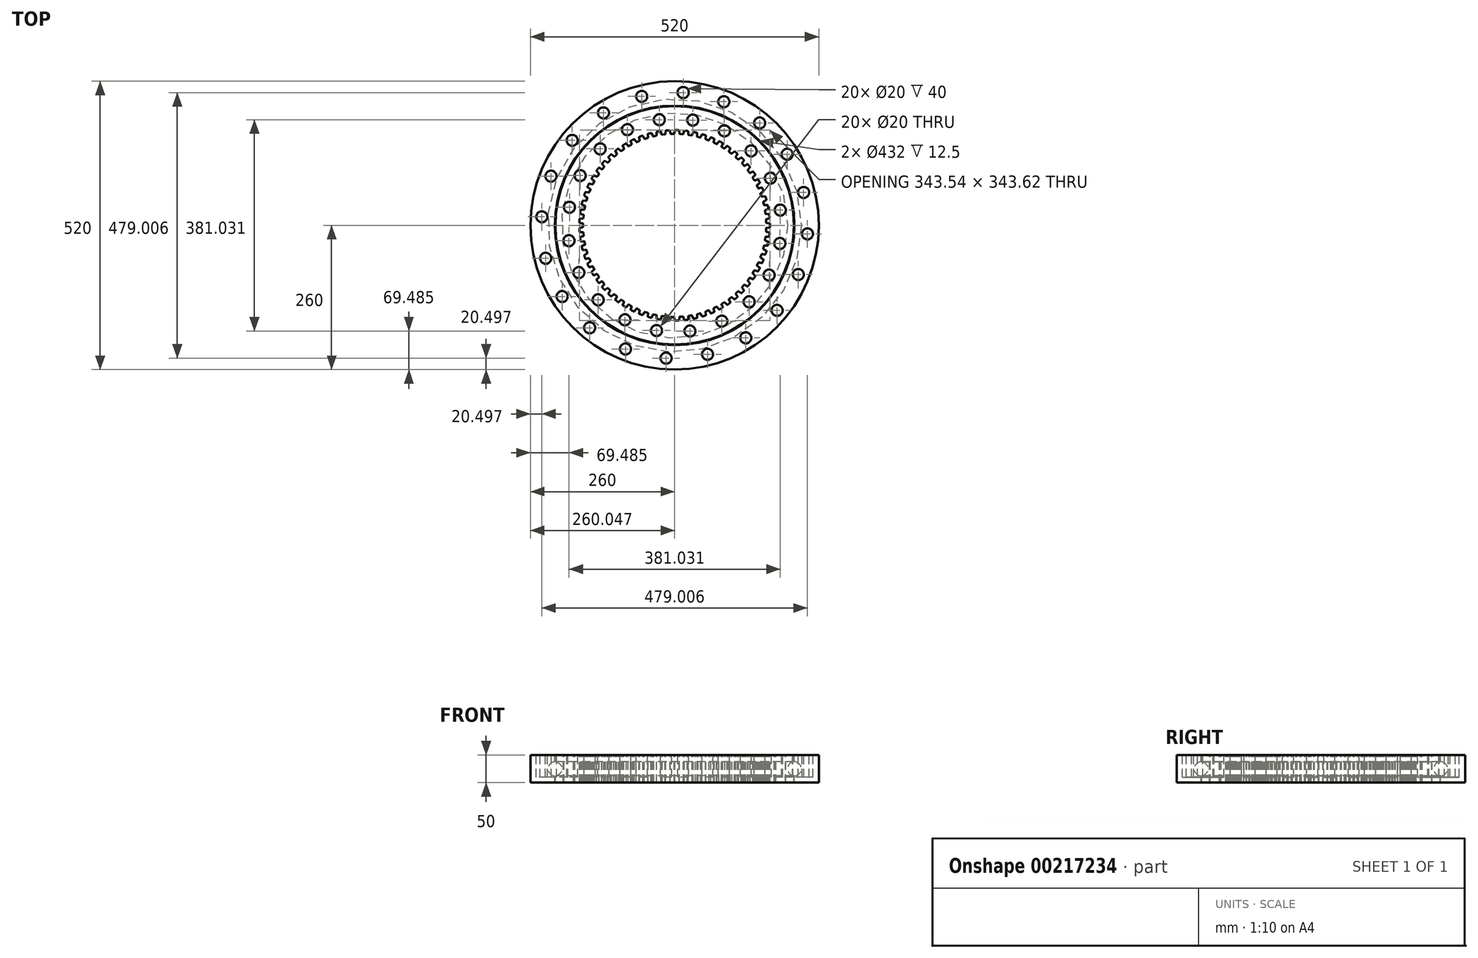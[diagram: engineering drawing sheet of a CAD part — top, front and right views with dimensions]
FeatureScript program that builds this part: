
annotation { "Feature Type Name" : "Feature", "Feature Type Description" : "" }
export const myFeature = defineFeature(function(context is Context, id is Id, definition is map)
    precondition{}
    {
        {
            var Q0;
            Q0=qCreatedBy(makeId("Front.planeOp"),FACE);
            var sketch = newSketch(context, id + "F0", { "sketchPlane" : qUnion([Q0])});
            skLineSegment(sketch, "E0.bottom", {"start": v(-260, 25) * mm, "end": v(-216, 25) * mm});
            skLineSegment(sketch, "E0.top", {"start": v(-260, -25) * mm, "end": v(-216, -25) * mm});
            skLineSegment(sketch, "E0.left", {"start": v(-260, 25) * mm, "end": v(-260, -25) * mm});
            skLineSegment(sketch, "E0.right", {"start": v(-216, 25) * mm, "end": v(-216, 12.5) * mm});
            skPoint(sketch, "E0.middle", {"position": v(-238, 0) * mm});
            skArc(sketch, "E1", {"start": v(-216, 12.5) * mm, "mid": v(-228.5, 0) * mm, "end": v(-216, -12.5) * mm});
            skLineSegment(sketch, "E2.bottom", {"start": v(-215, 25) * mm, "end": v(-172, 25) * mm});
            skLineSegment(sketch, "E2.top", {"start": v(-215, -25) * mm, "end": v(-172, -25) * mm});
            skLineSegment(sketch, "E2.left", {"start": v(-215, 25) * mm, "end": v(-215, 12.46) * mm});
            skLineSegment(sketch, "E2.right", {"start": v(-172, 25) * mm, "end": v(-172, -25) * mm});
            skPoint(sketch, "E2.middle", {"position": v(-193.5, 0) * mm});
            skArc(sketch, "E3.trimOffspring", {"start": v(-215, -12.46) * mm, "mid": v(-203.5, 0) * mm, "end": v(-215, 12.46) * mm});
            skLineSegment(sketch, "E4.trimOffspring", {"start": v(-215, -12.46) * mm, "end": v(-215, -25) * mm});
            skLineSegment(sketch, "E5.trimOffspring", {"start": v(-216, -12.5) * mm, "end": v(-216, -25) * mm});
            skLineSegment(sketch, "E6", {"start": v(0, 47.87) * mm, "end": v(0, -50.9) * mm, "construction": true});
            skSolve(sketch);
        }
        {
            var Q0;
            Q0=makeQuery(id+"F0.imprint","IMPRINT",FACE,{"disambiguationData":[TD([[makeQuery(id+"F0.imprint","IMPRINT",EDGE,{"derivedFrom":sQuery(id+"F0.wireOp",EDGE,"E0.bottom")}),-1.0]])]});
            var Q1;
            Q1=makeQuery(id+"F0.imprint","IMPRINT",FACE,{"disambiguationData":[TD([[makeQuery(id+"F0.imprint","IMPRINT",EDGE,{"derivedFrom":sQuery(id+"F0.wireOp",EDGE,"E2.bottom")}),-1.0]])]});
            var Q2;
            Q2=sQuery(id+"F0.wireOp",EDGE,"E6");
            revolve(context, id + "F1", {"entities" : qUnion([Q0, Q1]), "axis" : qUnion([Q2]), "revolveType" : RevolveType.FULL});
        }
        {
            var Q0;
            Q0=makeQuery(id+"F1.opRevolve","SWEPT_FACE",FACE,{"disambiguationData":[OSD([sQuery(id+"F0.wireOp",EDGE,"E0.bottom")])]});
            var sketch = newSketch(context, id + "F2", { "sketchPlane" : qUnion([Q0])});
            skCircle(sketch, "E7", {"center": v(0, 0) * mm, "radius": 240 * mm, "construction": true});
            skCircle(sketch, "E8", {"center": v(-239.5, 15.44) * mm, "radius": 10 * mm});
            skCircle(sketch, "E9.1.0", {"center": v(-232.55, -59.32) * mm, "radius": 10 * mm});
            skCircle(sketch, "E9.2.0", {"center": v(-202.84, -128.28) * mm, "radius": 10 * mm});
            skCircle(sketch, "E9.3.0", {"center": v(-153.27, -184.69) * mm, "radius": 10 * mm});
            skCircle(sketch, "E9.4.0", {"center": v(-88.7, -223) * mm, "radius": 10 * mm});
            skCircle(sketch, "E9.5.0", {"center": v(-15.44, -239.5) * mm, "radius": 10 * mm});
            skCircle(sketch, "E9.6.0", {"center": v(59.32, -232.55) * mm, "radius": 10 * mm});
            skCircle(sketch, "E9.7.0", {"center": v(128.28, -202.84) * mm, "radius": 10 * mm});
            skCircle(sketch, "E9.8.0", {"center": v(184.69, -153.27) * mm, "radius": 10 * mm});
            skCircle(sketch, "E9.9.0", {"center": v(223, -88.7) * mm, "radius": 10 * mm});
            skCircle(sketch, "E9.10.0", {"center": v(239.5, -15.44) * mm, "radius": 10 * mm});
            skCircle(sketch, "E9.11.0", {"center": v(232.55, 59.32) * mm, "radius": 10 * mm});
            skCircle(sketch, "E9.12.0", {"center": v(202.84, 128.28) * mm, "radius": 10 * mm});
            skCircle(sketch, "E9.13.0", {"center": v(153.27, 184.69) * mm, "radius": 10 * mm});
            skCircle(sketch, "E9.14.0", {"center": v(88.7, 223) * mm, "radius": 10 * mm});
            skCircle(sketch, "E9.15.0", {"center": v(15.44, 239.5) * mm, "radius": 10 * mm});
            skCircle(sketch, "E9.16.0", {"center": v(-59.32, 232.55) * mm, "radius": 10 * mm});
            skCircle(sketch, "E9.17.0", {"center": v(-128.28, 202.84) * mm, "radius": 10 * mm});
            skCircle(sketch, "E9.18.0", {"center": v(-184.69, 153.27) * mm, "radius": 10 * mm});
            skCircle(sketch, "E9.19.0", {"center": v(-223, 88.7) * mm, "radius": 10 * mm});
            skSolve(sketch);
        }
        {
            var Q0;
            Q0 = qSketchRegion(id + "F2", true);
            extrude(context, id + "F3", {"entities" : qUnion([Q0]), "operationType" : NewBodyOperationType.REMOVE, "oppositeDirection" : true, "depth" : 40 * mm});
        }
        {
            var Q0;
            Q0=makeQuery(id+"F1.opRevolve","SWEPT_FACE",FACE,{"disambiguationData":[OSD([sQuery(id+"F0.wireOp",EDGE,"E2.bottom")])]});
            var sketch = newSketch(context, id + "F4", { "sketchPlane" : qUnion([Q0])});
            skCircle(sketch, "E10", {"center": v(0, 0) * mm, "radius": 192.5 * mm, "construction": true});
            skCircle(sketch, "E11", {"center": v(-189.71, 32.65) * mm, "radius": 10 * mm});
            skCircle(sketch, "E12.1.0", {"center": v(-190.52, -27.57) * mm, "radius": 10 * mm});
            skCircle(sketch, "E12.2.0", {"center": v(-172.67, -85.1) * mm, "radius": 10 * mm});
            skCircle(sketch, "E12.3.0", {"center": v(-137.92, -134.29) * mm, "radius": 10 * mm});
            skCircle(sketch, "E12.4.0", {"center": v(-89.68, -170.34) * mm, "radius": 10 * mm});
            skCircle(sketch, "E12.5.0", {"center": v(-32.65, -189.71) * mm, "radius": 10 * mm});
            skCircle(sketch, "E12.6.0", {"center": v(27.57, -190.52) * mm, "radius": 10 * mm});
            skCircle(sketch, "E12.7.0", {"center": v(85.1, -172.67) * mm, "radius": 10 * mm});
            skCircle(sketch, "E12.8.0", {"center": v(134.29, -137.92) * mm, "radius": 10 * mm});
            skCircle(sketch, "E12.9.0", {"center": v(170.34, -89.68) * mm, "radius": 10 * mm});
            skCircle(sketch, "E12.10.0", {"center": v(189.71, -32.65) * mm, "radius": 10 * mm});
            skCircle(sketch, "E12.11.0", {"center": v(190.52, 27.57) * mm, "radius": 10 * mm});
            skCircle(sketch, "E12.12.0", {"center": v(172.67, 85.1) * mm, "radius": 10 * mm});
            skCircle(sketch, "E12.13.0", {"center": v(137.92, 134.29) * mm, "radius": 10 * mm});
            skCircle(sketch, "E12.14.0", {"center": v(89.68, 170.34) * mm, "radius": 10 * mm});
            skCircle(sketch, "E12.15.0", {"center": v(32.65, 189.71) * mm, "radius": 10 * mm});
            skCircle(sketch, "E12.16.0", {"center": v(-27.57, 190.52) * mm, "radius": 10 * mm});
            skCircle(sketch, "E12.17.0", {"center": v(-85.1, 172.67) * mm, "radius": 10 * mm});
            skCircle(sketch, "E12.18.0", {"center": v(-134.29, 137.92) * mm, "radius": 10 * mm});
            skCircle(sketch, "E12.19.0", {"center": v(-170.34, 89.68) * mm, "radius": 10 * mm});
            skSolve(sketch);
        }
        {
            var Q0;
            Q0 = qSketchRegion(id + "F4", true);
            extrude(context, id + "F5", {"entities" : qUnion([Q0]), "operationType" : NewBodyOperationType.REMOVE, "endBound" : BoundingType.THROUGH_ALL, "oppositeDirection" : true, "depth" : 25 * mm});
        }
        {
            var Q0;
            Q0=makeQuery(id+"F1.opRevolve","SWEPT_FACE",FACE,{"disambiguationData":[OSD([sQuery(id+"F0.wireOp",EDGE,"E2.bottom")])]});
            var sketch = newSketch(context, id + "F6", { "sketchPlane" : qUnion([Q0])});
            skLineSegment(sketch, "E13.left", {"start": v(-165.08, -2.5) * mm, "end": v(-165.08, 2.5) * mm});
            skPoint(sketch, "E13.middle", {"position": v(-168.03, 0) * mm});
            skArc(sketch, "E14", {"start": v(-171.72, -5.68) * mm, "mid": v(-171.62, -8.3) * mm, "end": v(-171.47, -10.92) * mm});
            skArc(sketch, "E15", {"start": v(-171.72, 5.68) * mm, "mid": v(-171.62, 5.05) * mm, "end": v(-171.29, 4.5) * mm});
            skPoint(sketch, "E16.visualSharp", {"position": v(-165.08, 5.92) * mm});
            skArc(sketch, "E16.filletArc", {"start": v(-165.08, 2.5) * mm, "mid": v(-165.38, 3.2) * mm, "end": v(-166.08, 3.5) * mm});
            skArc(sketch, "E17.filletArc", {"start": v(-166.08, -3.5) * mm, "mid": v(-165.38, -3.2) * mm, "end": v(-165.08, -2.5) * mm});
            skLineSegment(sketch, "E18", {"start": v(-170.94, 0) * mm, "end": v(-163.27, 0) * mm, "construction": true});
            skArc(sketch, "E19.MirrorCS", {"start": v(-171.72, -5.68) * mm, "mid": v(-171.62, -5.05) * mm, "end": v(-171.29, -4.5) * mm});
            skLineSegment(sketch, "E20", {"start": v(-171.29, 4.5) * mm, "end": v(-166.08, 3.5) * mm});
            skLineSegment(sketch, "E21", {"start": v(-171.29, -4.5) * mm, "end": v(-166.08, -3.5) * mm});
            skCircle(sketch, "E22", {"center": v(0, 0) * mm, "radius": 178.55 * mm});
            skPoint(sketch, "E23.1.0", {"position": v(-164.88, -10.04) * mm});
            skLineSegment(sketch, "E23.1.1", {"start": v(-170.92, -12.05) * mm, "end": v(-165.65, -12.55) * mm});
            skPoint(sketch, "E23.1.2", {"position": v(-164.2, -17.13) * mm});
            skArc(sketch, "E23.1.3", {"start": v(-170.37, -22.23) * mm, "mid": v(-170.33, -21.59) * mm, "end": v(-170.05, -21.01) * mm});
            skArc(sketch, "E23.1.4", {"start": v(-171.47, -10.92) * mm, "mid": v(-171.3, -11.54) * mm, "end": v(-170.92, -12.05) * mm});
            skPoint(sketch, "E23.1.5", {"position": v(-167.25, -16.22) * mm});
            skLineSegment(sketch, "E23.1.6", {"start": v(-170.05, -21.01) * mm, "end": v(-164.97, -19.51) * mm});
            skPoint(sketch, "E23.1.7", {"position": v(-169.6, -22.4) * mm});
            skPoint(sketch, "E23.1.8", {"position": v(-170.3, -15.3) * mm});
            skLineSegment(sketch, "E23.1.9", {"start": v(-164.07, -18.42) * mm, "end": v(-164.56, -13.44) * mm});
            skArc(sketch, "E23.1.10", {"start": v(-164.56, -13.44) * mm, "mid": v(-164.91, -12.77) * mm, "end": v(-165.65, -12.55) * mm});
            skArc(sketch, "E23.1.11", {"start": v(-164.97, -19.51) * mm, "mid": v(-164.3, -19.15) * mm, "end": v(-164.07, -18.42) * mm});
            skPoint(sketch, "E23.2.0", {"position": v(-163.15, -25.91) * mm});
            skLineSegment(sketch, "E23.2.1", {"start": v(-168.96, -28.5) * mm, "end": v(-163.66, -28.47) * mm});
            skPoint(sketch, "E23.2.2", {"position": v(-161.78, -32.9) * mm});
            skArc(sketch, "E23.2.3", {"start": v(-167.43, -38.57) * mm, "mid": v(-167.46, -37.93) * mm, "end": v(-167.23, -37.33) * mm});
            skArc(sketch, "E23.2.4", {"start": v(-169.62, -27.42) * mm, "mid": v(-169.4, -28.02) * mm, "end": v(-168.96, -28.5) * mm});
            skPoint(sketch, "E23.2.5", {"position": v(-164.9, -32.28) * mm});
            skLineSegment(sketch, "E23.2.6", {"start": v(-167.23, -37.33) * mm, "end": v(-162.32, -35.34) * mm});
            skPoint(sketch, "E23.2.7", {"position": v(-166.65, -38.66) * mm});
            skPoint(sketch, "E23.2.8", {"position": v(-168.02, -31.67) * mm});
            skLineSegment(sketch, "E23.2.9", {"start": v(-161.53, -34.17) * mm, "end": v(-162.49, -29.26) * mm});
            skArc(sketch, "E23.2.10", {"start": v(-162.49, -29.26) * mm, "mid": v(-162.91, -28.63) * mm, "end": v(-163.66, -28.47) * mm});
            skArc(sketch, "E23.2.11", {"start": v(-162.32, -35.34) * mm, "mid": v(-161.68, -34.92) * mm, "end": v(-161.53, -34.17) * mm});
            skPoint(sketch, "E23.3.0", {"position": v(-159.88, -41.54) * mm});
            skLineSegment(sketch, "E23.3.1", {"start": v(-165.42, -44.67) * mm, "end": v(-160.15, -44.14) * mm});
            skPoint(sketch, "E23.3.2", {"position": v(-157.85, -48.36) * mm});
            skArc(sketch, "E23.3.3", {"start": v(-162.93, -54.55) * mm, "mid": v(-163.01, -53.91) * mm, "end": v(-162.85, -53.3) * mm});
            skArc(sketch, "E23.3.4", {"start": v(-166.18, -43.66) * mm, "mid": v(-165.9, -44.24) * mm, "end": v(-165.42, -44.67) * mm});
            skPoint(sketch, "E23.3.5", {"position": v(-161.01, -48.05) * mm});
            skLineSegment(sketch, "E23.3.6", {"start": v(-162.85, -53.3) * mm, "end": v(-158.15, -50.84) * mm});
            skPoint(sketch, "E23.3.7", {"position": v(-162.14, -54.56) * mm});
            skPoint(sketch, "E23.3.8", {"position": v(-164.18, -47.74) * mm});
            skLineSegment(sketch, "E23.3.9", {"start": v(-157.48, -49.6) * mm, "end": v(-158.9, -44.8) * mm});
            skArc(sketch, "E23.3.10", {"start": v(-158.9, -44.8) * mm, "mid": v(-159.39, -44.22) * mm, "end": v(-160.15, -44.14) * mm});
            skArc(sketch, "E23.3.11", {"start": v(-158.15, -50.84) * mm, "mid": v(-157.56, -50.36) * mm, "end": v(-157.48, -49.6) * mm});
            skPoint(sketch, "E23.4.0", {"position": v(-155.13, -56.77) * mm});
            skLineSegment(sketch, "E23.4.1", {"start": v(-160.34, -60.42) * mm, "end": v(-155.14, -59.39) * mm});
            skPoint(sketch, "E23.4.2", {"position": v(-152.44, -63.37) * mm});
            skArc(sketch, "E23.4.3", {"start": v(-156.9, -70.02) * mm, "mid": v(-157.05, -69.4) * mm, "end": v(-156.95, -68.76) * mm});
            skArc(sketch, "E23.4.4", {"start": v(-161.19, -59.5) * mm, "mid": v(-160.86, -60.04) * mm, "end": v(-160.34, -60.42) * mm});
            skPoint(sketch, "E23.4.5", {"position": v(-155.63, -63.36) * mm});
            skLineSegment(sketch, "E23.4.6", {"start": v(-156.95, -68.76) * mm, "end": v(-152.5, -65.87) * mm});
            skPoint(sketch, "E23.4.7", {"position": v(-156.12, -69.95) * mm});
            skPoint(sketch, "E23.4.8", {"position": v(-158.8, -63.36) * mm});
            skLineSegment(sketch, "E23.4.9", {"start": v(-151.95, -64.57) * mm, "end": v(-153.84, -59.94) * mm});
            skArc(sketch, "E23.4.10", {"start": v(-153.84, -59.94) * mm, "mid": v(-154.38, -59.4) * mm, "end": v(-155.14, -59.39) * mm});
            skArc(sketch, "E23.4.11", {"start": v(-152.5, -65.87) * mm, "mid": v(-151.96, -65.33) * mm, "end": v(-151.95, -64.57) * mm});
            skPoint(sketch, "E23.5.0", {"position": v(-148.92, -71.48) * mm});
            skLineSegment(sketch, "E23.5.1", {"start": v(-153.76, -75.62) * mm, "end": v(-148.69, -74.08) * mm});
            skPoint(sketch, "E23.5.2", {"position": v(-145.62, -77.78) * mm});
            skArc(sketch, "E23.5.3", {"start": v(-149.41, -84.84) * mm, "mid": v(-149.62, -84.23) * mm, "end": v(-149.58, -83.59) * mm});
            skArc(sketch, "E23.5.4", {"start": v(-154.7, -74.77) * mm, "mid": v(-154.31, -75.29) * mm, "end": v(-153.76, -75.62) * mm});
            skPoint(sketch, "E23.5.5", {"position": v(-148.78, -78.09) * mm});
            skLineSegment(sketch, "E23.5.6", {"start": v(-149.58, -83.59) * mm, "end": v(-145.43, -80.28) * mm});
            skPoint(sketch, "E23.5.7", {"position": v(-148.64, -84.7) * mm});
            skPoint(sketch, "E23.5.8", {"position": v(-151.95, -78.4) * mm});
            skLineSegment(sketch, "E23.5.9", {"start": v(-145.01, -78.93) * mm, "end": v(-147.34, -74.5) * mm});
            skArc(sketch, "E23.5.10", {"start": v(-147.34, -74.5) * mm, "mid": v(-147.92, -74.01) * mm, "end": v(-148.69, -74.08) * mm});
            skArc(sketch, "E23.5.11", {"start": v(-145.43, -80.28) * mm, "mid": v(-144.94, -79.7) * mm, "end": v(-145.01, -78.93) * mm});
            skPoint(sketch, "E23.6.0", {"position": v(-141.33, -85.52) * mm});
            skLineSegment(sketch, "E23.6.1", {"start": v(-145.74, -90.1) * mm, "end": v(-140.84, -88.09) * mm});
            skPoint(sketch, "E23.6.2", {"position": v(-137.43, -91.47) * mm});
            skArc(sketch, "E23.6.3", {"start": v(-140.53, -98.86) * mm, "mid": v(-140.8, -98.27) * mm, "end": v(-140.81, -97.63) * mm});
            skArc(sketch, "E23.6.4", {"start": v(-146.76, -89.36) * mm, "mid": v(-146.32, -89.83) * mm, "end": v(-145.74, -90.1) * mm});
            skPoint(sketch, "E23.6.5", {"position": v(-140.55, -92.08) * mm});
            skLineSegment(sketch, "E23.6.6", {"start": v(-140.81, -97.63) * mm, "end": v(-137, -93.94) * mm});
            skPoint(sketch, "E23.6.7", {"position": v(-139.77, -98.65) * mm});
            skPoint(sketch, "E23.6.8", {"position": v(-143.67, -92.7) * mm});
            skLineSegment(sketch, "E23.6.9", {"start": v(-136.72, -92.56) * mm, "end": v(-139.46, -88.38) * mm});
            skArc(sketch, "E23.6.10", {"start": v(-139.46, -88.38) * mm, "mid": v(-140.1, -87.95) * mm, "end": v(-140.84, -88.09) * mm});
            skArc(sketch, "E23.6.11", {"start": v(-137, -93.94) * mm, "mid": v(-136.58, -93.31) * mm, "end": v(-136.72, -92.56) * mm});
            skPoint(sketch, "E23.7.0", {"position": v(-132.42, -98.76) * mm});
            skLineSegment(sketch, "E23.7.1", {"start": v(-136.37, -103.75) * mm, "end": v(-131.68, -101.27) * mm});
            skPoint(sketch, "E23.7.2", {"position": v(-127.96, -104.31) * mm});
            skArc(sketch, "E23.7.3", {"start": v(-130.33, -111.96) * mm, "mid": v(-130.65, -111.4) * mm, "end": v(-130.73, -110.77) * mm});
            skArc(sketch, "E23.7.4", {"start": v(-137.45, -103.1) * mm, "mid": v(-136.97, -103.53) * mm, "end": v(-136.37, -103.75) * mm});
            skPoint(sketch, "E23.7.5", {"position": v(-131, -105.22) * mm});
            skLineSegment(sketch, "E23.7.6", {"start": v(-130.73, -110.77) * mm, "end": v(-127.3, -106.73) * mm});
            skPoint(sketch, "E23.7.7", {"position": v(-129.6, -111.68) * mm});
            skPoint(sketch, "E23.7.8", {"position": v(-134.06, -106.13) * mm});
            skLineSegment(sketch, "E23.7.9", {"start": v(-127.15, -105.32) * mm, "end": v(-130.28, -101.42) * mm});
            skArc(sketch, "E23.7.10", {"start": v(-130.28, -101.42) * mm, "mid": v(-130.95, -101.06) * mm, "end": v(-131.68, -101.27) * mm});
            skArc(sketch, "E23.7.11", {"start": v(-127.3, -106.73) * mm, "mid": v(-126.93, -106.06) * mm, "end": v(-127.15, -105.32) * mm});
            skPoint(sketch, "E23.8.0", {"position": v(-122.27, -111.08) * mm});
            skLineSegment(sketch, "E23.8.1", {"start": v(-125.72, -116.43) * mm, "end": v(-121.3, -113.5) * mm});
            skPoint(sketch, "E23.8.2", {"position": v(-117.3, -116.17) * mm});
            skArc(sketch, "E23.8.3", {"start": v(-118.92, -124.02) * mm, "mid": v(-119.29, -123.5) * mm, "end": v(-119.43, -122.87) * mm});
            skArc(sketch, "E23.8.4", {"start": v(-126.85, -115.89) * mm, "mid": v(-126.34, -116.27) * mm, "end": v(-125.72, -116.43) * mm});
            skPoint(sketch, "E23.8.5", {"position": v(-120.24, -117.37) * mm});
            skLineSegment(sketch, "E23.8.6", {"start": v(-119.43, -122.87) * mm, "end": v(-116.4, -118.52) * mm});
            skPoint(sketch, "E23.8.7", {"position": v(-118.22, -123.66) * mm});
            skPoint(sketch, "E23.8.8", {"position": v(-123.19, -118.57) * mm});
            skLineSegment(sketch, "E23.8.9", {"start": v(-116.39, -117.1) * mm, "end": v(-119.88, -113.52) * mm});
            skArc(sketch, "E23.8.10", {"start": v(-119.88, -113.52) * mm, "mid": v(-120.58, -113.22) * mm, "end": v(-121.3, -113.5) * mm});
            skArc(sketch, "E23.8.11", {"start": v(-116.4, -118.52) * mm, "mid": v(-116.1, -117.81) * mm, "end": v(-116.39, -117.1) * mm});
            skPoint(sketch, "E23.9.0", {"position": v(-110.98, -122.36) * mm});
            skLineSegment(sketch, "E23.9.1", {"start": v(-113.9, -128.02) * mm, "end": v(-109.77, -124.68) * mm});
            skPoint(sketch, "E23.9.2", {"position": v(-105.53, -126.95) * mm});
            skArc(sketch, "E23.9.3", {"start": v(-106.4, -134.92) * mm, "mid": v(-106.81, -134.43) * mm, "end": v(-107.01, -133.82) * mm});
            skArc(sketch, "E23.9.4", {"start": v(-115.08, -127.59) * mm, "mid": v(-114.53, -127.92) * mm, "end": v(-113.9, -128.02) * mm});
            skPoint(sketch, "E23.9.5", {"position": v(-108.35, -128.43) * mm});
            skLineSegment(sketch, "E23.9.6", {"start": v(-107.01, -133.82) * mm, "end": v(-104.42, -129.2) * mm});
            skPoint(sketch, "E23.9.7", {"position": v(-105.73, -134.5) * mm});
            skPoint(sketch, "E23.9.8", {"position": v(-111.17, -129.9) * mm});
            skLineSegment(sketch, "E23.9.9", {"start": v(-104.54, -127.79) * mm, "end": v(-108.36, -124.56) * mm});
            skArc(sketch, "E23.9.10", {"start": v(-108.36, -124.56) * mm, "mid": v(-109.1, -124.33) * mm, "end": v(-109.77, -124.68) * mm});
            skArc(sketch, "E23.9.11", {"start": v(-104.42, -129.2) * mm, "mid": v(-104.2, -128.47) * mm, "end": v(-104.54, -127.79) * mm});
            skPoint(sketch, "E23.10.0", {"position": v(-98.65, -132.5) * mm});
            skLineSegment(sketch, "E23.10.1", {"start": v(-101, -138.41) * mm, "end": v(-97.23, -134.7) * mm});
            skPoint(sketch, "E23.10.2", {"position": v(-92.79, -136.54) * mm});
            skArc(sketch, "E23.10.3", {"start": v(-92.88, -144.55) * mm, "mid": v(-93.34, -144.11) * mm, "end": v(-93.6, -143.52) * mm});
            skArc(sketch, "E23.10.4", {"start": v(-102.23, -138.1) * mm, "mid": v(-101.65, -138.38) * mm, "end": v(-101, -138.41) * mm});
            skPoint(sketch, "E23.10.5", {"position": v(-95.45, -138.29) * mm});
            skLineSegment(sketch, "E23.10.6", {"start": v(-93.6, -143.52) * mm, "end": v(-91.47, -138.67) * mm});
            skPoint(sketch, "E23.10.7", {"position": v(-92.26, -144.07) * mm});
            skPoint(sketch, "E23.10.8", {"position": v(-98.11, -140.03) * mm});
            skLineSegment(sketch, "E23.10.9", {"start": v(-91.72, -137.28) * mm, "end": v(-95.84, -134.44) * mm});
            skArc(sketch, "E23.10.10", {"start": v(-95.84, -134.44) * mm, "mid": v(-96.58, -134.28) * mm, "end": v(-97.23, -134.7) * mm});
            skArc(sketch, "E23.10.11", {"start": v(-91.47, -138.67) * mm, "mid": v(-91.3, -137.92) * mm, "end": v(-91.72, -137.28) * mm});
            skPoint(sketch, "E23.11.0", {"position": v(-85.4, -141.4) * mm});
            skLineSegment(sketch, "E23.11.1", {"start": v(-87.18, -147.51) * mm, "end": v(-83.77, -143.45) * mm});
            skPoint(sketch, "E23.11.2", {"position": v(-79.18, -144.86) * mm});
            skArc(sketch, "E23.11.3", {"start": v(-78.5, -152.84) * mm, "mid": v(-79, -152.45) * mm, "end": v(-79.31, -151.89) * mm});
            skArc(sketch, "E23.11.4", {"start": v(-88.42, -147.32) * mm, "mid": v(-87.82, -147.54) * mm, "end": v(-87.18, -147.51) * mm});
            skPoint(sketch, "E23.11.5", {"position": v(-81.66, -146.85) * mm});
            skLineSegment(sketch, "E23.11.6", {"start": v(-79.31, -151.89) * mm, "end": v(-77.66, -146.85) * mm});
            skPoint(sketch, "E23.11.7", {"position": v(-77.92, -152.3) * mm});
            skPoint(sketch, "E23.11.8", {"position": v(-84.14, -148.84) * mm});
            skLineSegment(sketch, "E23.11.9", {"start": v(-78.04, -145.5) * mm, "end": v(-82.41, -143.06) * mm});
            skArc(sketch, "E23.11.10", {"start": v(-82.41, -143.06) * mm, "mid": v(-83.17, -142.98) * mm, "end": v(-83.77, -143.45) * mm});
            skArc(sketch, "E23.11.11", {"start": v(-77.66, -146.85) * mm, "mid": v(-77.57, -146.1) * mm, "end": v(-78.04, -145.5) * mm});
            skPoint(sketch, "E23.12.0", {"position": v(-71.35, -148.99) * mm});
            skLineSegment(sketch, "E23.12.1", {"start": v(-72.53, -155.24) * mm, "end": v(-69.54, -150.87) * mm});
            skPoint(sketch, "E23.12.2", {"position": v(-64.83, -151.83) * mm});
            skArc(sketch, "E23.12.3", {"start": v(-63.37, -159.7) * mm, "mid": v(-63.91, -159.36) * mm, "end": v(-64.28, -158.83) * mm});
            skArc(sketch, "E23.12.4", {"start": v(-73.79, -155.17) * mm, "mid": v(-73.17, -155.33) * mm, "end": v(-72.53, -155.24) * mm});
            skPoint(sketch, "E23.12.5", {"position": v(-67.1, -154.05) * mm});
            skLineSegment(sketch, "E23.12.6", {"start": v(-64.28, -158.83) * mm, "end": v(-63.12, -153.66) * mm});
            skPoint(sketch, "E23.12.7", {"position": v(-62.86, -159.11) * mm});
            skPoint(sketch, "E23.12.8", {"position": v(-69.38, -156.27) * mm});
            skLineSegment(sketch, "E23.12.9", {"start": v(-63.64, -152.35) * mm, "end": v(-68.22, -150.35) * mm});
            skArc(sketch, "E23.12.10", {"start": v(-68.22, -150.35) * mm, "mid": v(-68.99, -150.34) * mm, "end": v(-69.54, -150.87) * mm});
            skArc(sketch, "E23.12.11", {"start": v(-63.12, -153.66) * mm, "mid": v(-63.1, -152.9) * mm, "end": v(-63.64, -152.35) * mm});
            skPoint(sketch, "E23.13.0", {"position": v(-56.64, -155.18) * mm});
            skLineSegment(sketch, "E23.13.1", {"start": v(-57.21, -161.51) * mm, "end": v(-54.65, -156.87) * mm});
            skPoint(sketch, "E23.13.2", {"position": v(-49.87, -157.38) * mm});
            skArc(sketch, "E23.13.3", {"start": v(-47.66, -165.08) * mm, "mid": v(-48.23, -164.78) * mm, "end": v(-48.65, -164.3) * mm});
            skArc(sketch, "E23.13.4", {"start": v(-58.47, -161.56) * mm, "mid": v(-57.84, -161.66) * mm, "end": v(-57.21, -161.51) * mm});
            skPoint(sketch, "E23.13.5", {"position": v(-51.92, -159.8) * mm});
            skLineSegment(sketch, "E23.13.6", {"start": v(-48.65, -164.3) * mm, "end": v(-48, -159.04) * mm});
            skPoint(sketch, "E23.13.7", {"position": v(-47.2, -164.44) * mm});
            skPoint(sketch, "E23.13.8", {"position": v(-53.98, -162.24) * mm});
            skLineSegment(sketch, "E23.13.9", {"start": v(-48.64, -157.78) * mm, "end": v(-53.4, -156.23) * mm});
            skArc(sketch, "E23.13.10", {"start": v(-53.4, -156.23) * mm, "mid": v(-54.15, -156.3) * mm, "end": v(-54.65, -156.87) * mm});
            skArc(sketch, "E23.13.11", {"start": v(-48, -159.04) * mm, "mid": v(-48.05, -158.27) * mm, "end": v(-48.64, -157.78) * mm});
            skPoint(sketch, "E23.14.0", {"position": v(-41.4, -159.92) * mm});
            skLineSegment(sketch, "E23.14.1", {"start": v(-41.36, -166.28) * mm, "end": v(-39.26, -161.42) * mm});
            skPoint(sketch, "E23.14.2", {"position": v(-34.45, -161.45) * mm});
            skArc(sketch, "E23.14.3", {"start": v(-31.5, -168.9) * mm, "mid": v(-32.1, -168.67) * mm, "end": v(-32.57, -168.22) * mm});
            skArc(sketch, "E23.14.4", {"start": v(-42.6, -166.45) * mm, "mid": v(-41.96, -166.5) * mm, "end": v(-41.36, -166.28) * mm});
            skPoint(sketch, "E23.14.5", {"position": v(-36.26, -164.07) * mm});
            skLineSegment(sketch, "E23.14.6", {"start": v(-32.57, -168.22) * mm, "end": v(-32.42, -162.93) * mm});
            skPoint(sketch, "E23.14.7", {"position": v(-31.12, -168.22) * mm});
            skPoint(sketch, "E23.14.8", {"position": v(-38.07, -166.69) * mm});
            skLineSegment(sketch, "E23.14.9", {"start": v(-33.18, -161.73) * mm, "end": v(-38.06, -160.66) * mm});
            skArc(sketch, "E23.14.10", {"start": v(-38.06, -160.66) * mm, "mid": v(-38.82, -160.79) * mm, "end": v(-39.26, -161.42) * mm});
            skArc(sketch, "E23.14.11", {"start": v(-32.42, -162.93) * mm, "mid": v(-32.55, -162.17) * mm, "end": v(-33.18, -161.73) * mm});
            skPoint(sketch, "E23.15.0", {"position": v(-25.77, -163.17) * mm});
            skLineSegment(sketch, "E23.15.1", {"start": v(-25.11, -169.5) * mm, "end": v(-23.5, -164.45) * mm});
            skPoint(sketch, "E23.15.2", {"position": v(-18.7, -164.03) * mm});
            skArc(sketch, "E23.15.3", {"start": v(-15.06, -171.16) * mm, "mid": v(-15.68, -170.98) * mm, "end": v(-16.18, -170.58) * mm});
            skArc(sketch, "E23.15.4", {"start": v(-26.34, -169.79) * mm, "mid": v(-25.7, -169.76) * mm, "end": v(-25.11, -169.5) * mm});
            skPoint(sketch, "E23.15.5", {"position": v(-20.25, -166.8) * mm});
            skLineSegment(sketch, "E23.15.6", {"start": v(-16.18, -170.58) * mm, "end": v(-16.54, -165.3) * mm});
            skPoint(sketch, "E23.15.7", {"position": v(-14.73, -170.44) * mm});
            skPoint(sketch, "E23.15.8", {"position": v(-21.8, -169.58) * mm});
            skLineSegment(sketch, "E23.15.9", {"start": v(-17.42, -164.18) * mm, "end": v(-22.38, -163.58) * mm});
            skArc(sketch, "E23.15.10", {"start": v(-22.38, -163.58) * mm, "mid": v(-23.12, -163.78) * mm, "end": v(-23.5, -164.45) * mm});
            skArc(sketch, "E23.15.11", {"start": v(-16.54, -165.3) * mm, "mid": v(-16.75, -164.56) * mm, "end": v(-17.42, -164.18) * mm});
            skPoint(sketch, "E23.16.0", {"position": v(-9.9, -164.9) * mm});
            skLineSegment(sketch, "E23.16.1", {"start": v(-8.64, -171.13) * mm, "end": v(-7.51, -165.95) * mm});
            skPoint(sketch, "E23.16.2", {"position": v(-2.79, -165.07) * mm});
            skArc(sketch, "E23.16.3", {"start": v(1.53, -171.81) * mm, "mid": v(0.9, -171.7) * mm, "end": v(0.36, -171.35) * mm});
            skArc(sketch, "E23.16.4", {"start": v(-9.83, -171.54) * mm, "mid": v(-9.2, -171.45) * mm, "end": v(-8.64, -171.13) * mm});
            skPoint(sketch, "E23.16.5", {"position": v(-4.06, -167.98) * mm});
            skLineSegment(sketch, "E23.16.6", {"start": v(0.36, -171.35) * mm, "end": v(-0.51, -166.12) * mm});
            skPoint(sketch, "E23.16.7", {"position": v(1.78, -171.07) * mm});
            skPoint(sketch, "E23.16.8", {"position": v(-5.33, -170.9) * mm});
            skLineSegment(sketch, "E23.16.9", {"start": v(-1.49, -165.1) * mm, "end": v(-6.49, -164.98) * mm});
            skArc(sketch, "E23.16.10", {"start": v(-6.49, -164.98) * mm, "mid": v(-7.2, -165.25) * mm, "end": v(-7.51, -165.95) * mm});
            skArc(sketch, "E23.16.11", {"start": v(-0.51, -166.12) * mm, "mid": v(-0.79, -165.4) * mm, "end": v(-1.49, -165.1) * mm});
            skPoint(sketch, "E23.17.0", {"position": v(6.06, -165.08) * mm});
            skLineSegment(sketch, "E23.17.1", {"start": v(7.92, -171.16) * mm, "end": v(8.54, -165.9) * mm});
            skPoint(sketch, "E23.17.2", {"position": v(13.16, -164.56) * mm});
            skArc(sketch, "E23.17.3", {"start": v(18.1, -170.86) * mm, "mid": v(17.47, -170.8) * mm, "end": v(16.9, -170.51) * mm});
            skArc(sketch, "E23.17.4", {"start": v(6.77, -171.69) * mm, "mid": v(7.4, -171.54) * mm, "end": v(7.92, -171.16) * mm});
            skPoint(sketch, "E23.17.5", {"position": v(12.17, -167.59) * mm});
            skLineSegment(sketch, "E23.17.6", {"start": v(16.9, -170.51) * mm, "end": v(15.52, -165.4) * mm});
            skPoint(sketch, "E23.17.7", {"position": v(18.29, -170.1) * mm});
            skPoint(sketch, "E23.17.8", {"position": v(11.19, -170.61) * mm});
            skLineSegment(sketch, "E23.17.9", {"start": v(14.45, -164.47) * mm, "end": v(9.46, -164.83) * mm});
            skArc(sketch, "E23.17.10", {"start": v(9.46, -164.83) * mm, "mid": v(8.78, -165.18) * mm, "end": v(8.54, -165.9) * mm});
            skArc(sketch, "E23.17.11", {"start": v(15.52, -165.4) * mm, "mid": v(15.18, -164.71) * mm, "end": v(14.45, -164.47) * mm});
            skPoint(sketch, "E23.18.0", {"position": v(21.96, -163.72) * mm});
            skLineSegment(sketch, "E23.18.1", {"start": v(24.4, -169.6) * mm, "end": v(24.51, -164.3) * mm});
            skPoint(sketch, "E23.18.2", {"position": v(28.98, -162.53) * mm});
            skArc(sketch, "E23.18.3", {"start": v(34.51, -168.32) * mm, "mid": v(33.87, -168.32) * mm, "end": v(33.27, -168.09) * mm});
            skArc(sketch, "E23.18.4", {"start": v(23.31, -170.23) * mm, "mid": v(23.92, -170.02) * mm, "end": v(24.4, -169.6) * mm});
            skPoint(sketch, "E23.18.5", {"position": v(28.29, -165.63) * mm});
            skLineSegment(sketch, "E23.18.6", {"start": v(33.27, -168.09) * mm, "end": v(31.41, -163.12) * mm});
            skPoint(sketch, "E23.18.7", {"position": v(34.62, -167.54) * mm});
            skPoint(sketch, "E23.18.8", {"position": v(27.6, -168.74) * mm});
            skLineSegment(sketch, "E23.18.9", {"start": v(30.26, -162.3) * mm, "end": v(25.33, -163.15) * mm});
            skArc(sketch, "E23.18.10", {"start": v(25.33, -163.15) * mm, "mid": v(24.68, -163.56) * mm, "end": v(24.51, -164.3) * mm});
            skArc(sketch, "E23.18.11", {"start": v(31.41, -163.12) * mm, "mid": v(31, -162.48) * mm, "end": v(30.26, -162.3) * mm});
            skPoint(sketch, "E23.19.0", {"position": v(37.66, -160.84) * mm});
            skLineSegment(sketch, "E23.19.1", {"start": v(40.66, -166.45) * mm, "end": v(40.25, -161.17) * mm});
            skPoint(sketch, "E23.19.2", {"position": v(44.53, -158.97) * mm});
            skArc(sketch, "E23.19.3", {"start": v(50.6, -164.2) * mm, "mid": v(49.96, -164.27) * mm, "end": v(49.34, -164.1) * mm});
            skArc(sketch, "E23.19.4", {"start": v(39.63, -167.19) * mm, "mid": v(40.22, -166.92) * mm, "end": v(40.66, -166.45) * mm});
            skPoint(sketch, "E23.19.5", {"position": v(44.14, -162.13) * mm});
            skLineSegment(sketch, "E23.19.6", {"start": v(49.34, -164.1) * mm, "end": v(47, -159.33) * mm});
            skPoint(sketch, "E23.19.7", {"position": v(50.63, -163.42) * mm});
            skPoint(sketch, "E23.19.8", {"position": v(43.76, -165.29) * mm});
            skLineSegment(sketch, "E23.19.9", {"start": v(45.78, -158.63) * mm, "end": v(40.96, -159.94) * mm});
            skArc(sketch, "E23.19.10", {"start": v(40.96, -159.94) * mm, "mid": v(40.35, -160.41) * mm, "end": v(40.25, -161.17) * mm});
            skArc(sketch, "E23.19.11", {"start": v(47, -159.33) * mm, "mid": v(46.54, -158.73) * mm, "end": v(45.78, -158.63) * mm});
            skPoint(sketch, "E23.20.0", {"position": v(53, -156.45) * mm});
            skLineSegment(sketch, "E23.20.1", {"start": v(56.53, -161.75) * mm, "end": v(55.62, -156.53) * mm});
            skPoint(sketch, "E23.20.2", {"position": v(59.66, -153.93) * mm});
            skArc(sketch, "E23.20.3", {"start": v(66.2, -158.55) * mm, "mid": v(65.58, -158.68) * mm, "end": v(64.95, -158.56) * mm});
            skArc(sketch, "E23.20.4", {"start": v(55.58, -162.58) * mm, "mid": v(56.14, -162.26) * mm, "end": v(56.53, -161.75) * mm});
            skPoint(sketch, "E23.20.5", {"position": v(59.58, -157.11) * mm});
            skLineSegment(sketch, "E23.20.6", {"start": v(64.95, -158.56) * mm, "end": v(62.17, -154.05) * mm});
            skPoint(sketch, "E23.20.7", {"position": v(66.16, -157.77) * mm});
            skPoint(sketch, "E23.20.8", {"position": v(59.5, -160.3) * mm});
            skLineSegment(sketch, "E23.20.9", {"start": v(60.88, -153.47) * mm, "end": v(56.2, -155.24) * mm});
            skArc(sketch, "E23.20.10", {"start": v(56.2, -155.24) * mm, "mid": v(55.64, -155.77) * mm, "end": v(55.62, -156.53) * mm});
            skArc(sketch, "E23.20.11", {"start": v(62.17, -154.05) * mm, "mid": v(61.64, -153.5) * mm, "end": v(60.88, -153.47) * mm});
            skPoint(sketch, "E23.21.0", {"position": v(67.86, -150.6) * mm});
            skLineSegment(sketch, "E23.21.1", {"start": v(71.88, -155.54) * mm, "end": v(70.47, -150.43) * mm});
            skPoint(sketch, "E23.21.2", {"position": v(74.24, -147.45) * mm});
            skArc(sketch, "E23.21.3", {"start": v(81.2, -151.42) * mm, "mid": v(80.59, -151.6) * mm, "end": v(79.95, -151.55) * mm});
            skArc(sketch, "E23.21.4", {"start": v(71.01, -156.46) * mm, "mid": v(71.54, -156.08) * mm, "end": v(71.88, -155.54) * mm});
            skPoint(sketch, "E23.21.5", {"position": v(74.47, -150.63) * mm});
            skLineSegment(sketch, "E23.21.6", {"start": v(79.95, -151.55) * mm, "end": v(76.74, -147.33) * mm});
            skPoint(sketch, "E23.21.7", {"position": v(81.08, -150.64) * mm});
            skPoint(sketch, "E23.21.8", {"position": v(74.7, -153.8) * mm});
            skLineSegment(sketch, "E23.21.9", {"start": v(75.4, -146.88) * mm, "end": v(70.92, -149.1) * mm});
            skArc(sketch, "E23.21.10", {"start": v(70.92, -149.1) * mm, "mid": v(70.42, -149.67) * mm, "end": v(70.47, -150.43) * mm});
            skArc(sketch, "E23.21.11", {"start": v(76.74, -147.33) * mm, "mid": v(76.17, -146.83) * mm, "end": v(75.4, -146.88) * mm});
            skPoint(sketch, "E23.22.0", {"position": v(82.08, -143.36) * mm});
            skLineSegment(sketch, "E23.22.1", {"start": v(86.56, -147.88) * mm, "end": v(84.66, -142.93) * mm});
            skPoint(sketch, "E23.22.2", {"position": v(88.13, -139.6) * mm});
            skArc(sketch, "E23.22.3", {"start": v(95.44, -142.88) * mm, "mid": v(94.84, -143.12) * mm, "end": v(94.2, -143.13) * mm});
            skArc(sketch, "E23.22.4", {"start": v(85.78, -148.87) * mm, "mid": v(86.27, -148.45) * mm, "end": v(86.56, -147.88) * mm});
            skPoint(sketch, "E23.22.5", {"position": v(88.66, -142.74) * mm});
            skLineSegment(sketch, "E23.22.6", {"start": v(94.2, -143.13) * mm, "end": v(90.6, -139.24) * mm});
            skPoint(sketch, "E23.22.7", {"position": v(95.24, -142.12) * mm});
            skPoint(sketch, "E23.22.8", {"position": v(89.2, -145.87) * mm});
            skLineSegment(sketch, "E23.22.9", {"start": v(89.23, -138.91) * mm, "end": v(84.98, -141.55) * mm});
            skArc(sketch, "E23.22.10", {"start": v(84.98, -141.55) * mm, "mid": v(84.54, -142.17) * mm, "end": v(84.66, -142.93) * mm});
            skArc(sketch, "E23.22.11", {"start": v(90.6, -139.24) * mm, "mid": v(89.98, -138.8) * mm, "end": v(89.23, -138.91) * mm});
            skPoint(sketch, "E23.23.0", {"position": v(95.53, -134.77) * mm});
            skLineSegment(sketch, "E23.23.1", {"start": v(100.42, -138.83) * mm, "end": v(98.06, -134.1) * mm});
            skPoint(sketch, "E23.23.2", {"position": v(101.19, -130.44) * mm});
            skArc(sketch, "E23.23.3", {"start": v(108.78, -133) * mm, "mid": v(108.21, -133.3) * mm, "end": v(107.58, -133.37) * mm});
            skArc(sketch, "E23.23.4", {"start": v(99.75, -139.9) * mm, "mid": v(100.2, -139.43) * mm, "end": v(100.42, -138.83) * mm});
            skPoint(sketch, "E23.23.5", {"position": v(102.02, -133.51) * mm});
            skLineSegment(sketch, "E23.23.6", {"start": v(107.58, -133.37) * mm, "end": v(103.62, -129.84) * mm});
            skPoint(sketch, "E23.23.7", {"position": v(108.51, -132.26) * mm});
            skPoint(sketch, "E23.23.8", {"position": v(102.86, -136.58) * mm});
            skLineSegment(sketch, "E23.23.9", {"start": v(102.22, -129.65) * mm, "end": v(98.25, -132.7) * mm});
            skArc(sketch, "E23.23.10", {"start": v(98.25, -132.7) * mm, "mid": v(97.86, -133.35) * mm, "end": v(98.06, -134.1) * mm});
            skArc(sketch, "E23.23.11", {"start": v(103.62, -129.84) * mm, "mid": v(102.96, -129.46) * mm, "end": v(102.22, -129.65) * mm});
            skPoint(sketch, "E23.24.0", {"position": v(108.1, -124.92) * mm});
            skLineSegment(sketch, "E23.24.1", {"start": v(113.36, -128.5) * mm, "end": v(110.54, -124) * mm});
            skPoint(sketch, "E23.24.2", {"position": v(113.3, -120.07) * mm});
            skArc(sketch, "E23.24.3", {"start": v(121.1, -121.88) * mm, "mid": v(120.57, -122.24) * mm, "end": v(119.95, -122.36) * mm});
            skArc(sketch, "E23.24.4", {"start": v(112.79, -129.62) * mm, "mid": v(113.18, -129.11) * mm, "end": v(113.36, -128.5) * mm});
            skPoint(sketch, "E23.24.5", {"position": v(114.43, -123.04) * mm});
            skLineSegment(sketch, "E23.24.6", {"start": v(119.95, -122.36) * mm, "end": v(115.67, -119.23) * mm});
            skPoint(sketch, "E23.24.7", {"position": v(120.77, -121.17) * mm});
            skPoint(sketch, "E23.24.8", {"position": v(115.56, -126.02) * mm});
            skLineSegment(sketch, "E23.24.9", {"start": v(114.26, -119.18) * mm, "end": v(110.6, -122.59) * mm});
            skArc(sketch, "E23.24.10", {"start": v(110.6, -122.59) * mm, "mid": v(110.28, -123.28) * mm, "end": v(110.54, -124) * mm});
            skArc(sketch, "E23.24.11", {"start": v(115.67, -119.23) * mm, "mid": v(114.97, -118.92) * mm, "end": v(114.26, -119.18) * mm});
            skPoint(sketch, "E23.25.0", {"position": v(119.64, -113.9) * mm});
            skLineSegment(sketch, "E23.25.1", {"start": v(125.23, -116.95) * mm, "end": v(122, -112.75) * mm});
            skPoint(sketch, "E23.25.2", {"position": v(124.36, -108.57) * mm});
            skArc(sketch, "E23.25.3", {"start": v(132.3, -109.62) * mm, "mid": v(131.8, -110.03) * mm, "end": v(131.2, -110.22) * mm});
            skArc(sketch, "E23.25.4", {"start": v(124.77, -118.13) * mm, "mid": v(125.11, -117.59) * mm, "end": v(125.23, -116.95) * mm});
            skPoint(sketch, "E23.25.5", {"position": v(125.77, -111.42) * mm});
            skLineSegment(sketch, "E23.25.6", {"start": v(131.2, -110.22) * mm, "end": v(126.64, -107.51) * mm});
            skPoint(sketch, "E23.25.7", {"position": v(131.9, -108.95) * mm});
            skPoint(sketch, "E23.25.8", {"position": v(127.18, -114.28) * mm});
            skLineSegment(sketch, "E23.25.9", {"start": v(125.23, -107.6) * mm, "end": v(121.9, -111.34) * mm});
            skArc(sketch, "E23.25.10", {"start": v(121.9, -111.34) * mm, "mid": v(121.66, -112.07) * mm, "end": v(122, -112.75) * mm});
            skArc(sketch, "E23.25.11", {"start": v(126.64, -107.51) * mm, "mid": v(125.91, -107.26) * mm, "end": v(125.23, -107.6) * mm});
            skPoint(sketch, "E23.26.0", {"position": v(130.08, -101.82) * mm});
            skLineSegment(sketch, "E23.26.1", {"start": v(135.93, -104.32) * mm, "end": v(132.3, -100.45) * mm});
            skPoint(sketch, "E23.26.2", {"position": v(134.26, -96.06) * mm});
            skArc(sketch, "E23.26.3", {"start": v(142.27, -96.34) * mm, "mid": v(141.81, -96.8) * mm, "end": v(141.22, -97.04) * mm});
            skArc(sketch, "E23.26.4", {"start": v(135.59, -105.53) * mm, "mid": v(135.88, -104.96) * mm, "end": v(135.93, -104.32) * mm});
            skPoint(sketch, "E23.26.5", {"position": v(135.94, -98.77) * mm});
            skLineSegment(sketch, "E23.26.6", {"start": v(141.22, -97.04) * mm, "end": v(136.42, -94.8) * mm});
            skPoint(sketch, "E23.26.7", {"position": v(141.8, -95.7) * mm});
            skPoint(sketch, "E23.26.8", {"position": v(137.62, -101.47) * mm});
            skLineSegment(sketch, "E23.26.9", {"start": v(135.03, -95.01) * mm, "end": v(132.09, -99.06) * mm});
            skArc(sketch, "E23.26.10", {"start": v(132.09, -99.06) * mm, "mid": v(131.9, -99.8) * mm, "end": v(132.3, -100.45) * mm});
            skArc(sketch, "E23.26.11", {"start": v(136.42, -94.8) * mm, "mid": v(135.68, -94.61) * mm, "end": v(135.03, -95.01) * mm});
            skPoint(sketch, "E23.27.0", {"position": v(139.3, -88.8) * mm});
            skLineSegment(sketch, "E23.27.1", {"start": v(145.36, -90.72) * mm, "end": v(141.39, -87.22) * mm});
            skPoint(sketch, "E23.27.2", {"position": v(142.9, -82.66) * mm});
            skArc(sketch, "E23.27.3", {"start": v(150.9, -82.16) * mm, "mid": v(150.5, -82.65) * mm, "end": v(149.93, -82.96) * mm});
            skArc(sketch, "E23.27.4", {"start": v(145.14, -91.95) * mm, "mid": v(145.37, -91.36) * mm, "end": v(145.36, -90.72) * mm});
            skPoint(sketch, "E23.27.5", {"position": v(144.84, -85.18) * mm});
            skLineSegment(sketch, "E23.27.6", {"start": v(149.93, -82.96) * mm, "end": v(144.93, -81.18) * mm});
            skPoint(sketch, "E23.27.7", {"position": v(150.38, -81.58) * mm});
            skPoint(sketch, "E23.27.8", {"position": v(146.77, -87.71) * mm});
            skLineSegment(sketch, "E23.27.9", {"start": v(143.57, -81.54) * mm, "end": v(141.03, -85.85) * mm});
            skArc(sketch, "E23.27.10", {"start": v(141.03, -85.85) * mm, "mid": v(140.92, -86.6) * mm, "end": v(141.39, -87.22) * mm});
            skArc(sketch, "E23.27.11", {"start": v(144.93, -81.18) * mm, "mid": v(144.18, -81.08) * mm, "end": v(143.57, -81.54) * mm});
            skPoint(sketch, "E23.28.0", {"position": v(147.22, -74.93) * mm});
            skLineSegment(sketch, "E23.28.1", {"start": v(153.44, -76.26) * mm, "end": v(149.14, -73.16) * mm});
            skPoint(sketch, "E23.28.2", {"position": v(150.22, -68.48) * mm});
            skArc(sketch, "E23.28.3", {"start": v(158.13, -67.21) * mm, "mid": v(157.77, -67.74) * mm, "end": v(157.23, -68.1) * mm});
            skArc(sketch, "E23.28.4", {"start": v(153.34, -77.52) * mm, "mid": v(153.51, -76.9) * mm, "end": v(153.44, -76.26) * mm});
            skPoint(sketch, "E23.28.5", {"position": v(152.38, -70.8) * mm});
            skLineSegment(sketch, "E23.28.6", {"start": v(157.23, -68.1) * mm, "end": v(152.1, -66.81) * mm});
            skPoint(sketch, "E23.28.7", {"position": v(157.55, -66.68) * mm});
            skPoint(sketch, "E23.28.8", {"position": v(154.55, -73.14) * mm});
            skLineSegment(sketch, "E23.28.9", {"start": v(150.76, -67.3) * mm, "end": v(148.66, -71.83) * mm});
            skArc(sketch, "E23.28.10", {"start": v(148.66, -71.83) * mm, "mid": v(148.62, -72.6) * mm, "end": v(149.14, -73.16) * mm});
            skArc(sketch, "E23.28.11", {"start": v(152.1, -66.81) * mm, "mid": v(151.33, -66.78) * mm, "end": v(150.76, -67.3) * mm});
            skPoint(sketch, "E23.29.0", {"position": v(153.76, -60.37) * mm});
            skLineSegment(sketch, "E23.29.1", {"start": v(160.09, -61.1) * mm, "end": v(155.5, -58.43) * mm});
            skPoint(sketch, "E23.29.2", {"position": v(156.12, -53.66) * mm});
            skArc(sketch, "E23.29.3", {"start": v(163.88, -51.64) * mm, "mid": v(163.57, -52.2) * mm, "end": v(163.07, -52.6) * mm});
            skArc(sketch, "E23.29.4", {"start": v(160.1, -62.36) * mm, "mid": v(160.22, -61.72) * mm, "end": v(160.09, -61.1) * mm});
            skPoint(sketch, "E23.29.5", {"position": v(158.5, -55.77) * mm});
            skLineSegment(sketch, "E23.29.6", {"start": v(163.07, -52.6) * mm, "end": v(157.83, -51.82) * mm});
            skPoint(sketch, "E23.29.7", {"position": v(163.25, -51.17) * mm});
            skPoint(sketch, "E23.29.8", {"position": v(160.88, -57.88) * mm});
            skLineSegment(sketch, "E23.29.9", {"start": v(156.56, -52.43) * mm, "end": v(154.9, -57.15) * mm});
            skArc(sketch, "E23.29.10", {"start": v(154.9, -57.15) * mm, "mid": v(154.94, -57.92) * mm, "end": v(155.5, -58.43) * mm});
            skArc(sketch, "E23.29.11", {"start": v(157.83, -51.82) * mm, "mid": v(157.07, -51.86) * mm, "end": v(156.56, -52.43) * mm});
            skPoint(sketch, "E23.30.0", {"position": v(158.87, -45.25) * mm});
            skLineSegment(sketch, "E23.30.1", {"start": v(165.23, -45.36) * mm, "end": v(160.42, -43.14) * mm});
            skPoint(sketch, "E23.30.2", {"position": v(160.57, -38.34) * mm});
            skArc(sketch, "E23.30.3", {"start": v(168.1, -35.58) * mm, "mid": v(167.84, -36.17) * mm, "end": v(167.39, -36.62) * mm});
            skArc(sketch, "E23.30.4", {"start": v(165.38, -46.61) * mm, "mid": v(165.43, -45.97) * mm, "end": v(165.23, -45.36) * mm});
            skPoint(sketch, "E23.30.5", {"position": v(163.15, -40.21) * mm});
            skLineSegment(sketch, "E23.30.6", {"start": v(167.39, -36.62) * mm, "end": v(162.1, -36.35) * mm});
            skPoint(sketch, "E23.30.7", {"position": v(167.42, -35.17) * mm});
            skPoint(sketch, "E23.30.8", {"position": v(165.72, -42.08) * mm});
            skLineSegment(sketch, "E23.30.9", {"start": v(160.89, -37.08) * mm, "end": v(159.69, -41.93) * mm});
            skArc(sketch, "E23.30.10", {"start": v(159.69, -41.93) * mm, "mid": v(159.8, -42.7) * mm, "end": v(160.42, -43.14) * mm});
            skArc(sketch, "E23.30.11", {"start": v(162.1, -36.35) * mm, "mid": v(161.34, -36.46) * mm, "end": v(160.89, -37.08) * mm});
            skPoint(sketch, "E23.31.0", {"position": v(162.5, -29.7) * mm});
            skLineSegment(sketch, "E23.31.1", {"start": v(168.84, -29.2) * mm, "end": v(163.84, -27.46) * mm});
            skPoint(sketch, "E23.31.2", {"position": v(163.53, -22.66) * mm});
            skArc(sketch, "E23.31.3", {"start": v(170.74, -19.2) * mm, "mid": v(170.55, -19.8) * mm, "end": v(170.14, -20.3) * mm});
            skArc(sketch, "E23.31.4", {"start": v(169.1, -30.43) * mm, "mid": v(169.1, -29.8) * mm, "end": v(168.84, -29.2) * mm});
            skPoint(sketch, "E23.31.5", {"position": v(166.27, -24.28) * mm});
            skLineSegment(sketch, "E23.31.6", {"start": v(170.14, -20.3) * mm, "end": v(164.85, -20.53) * mm});
            skPoint(sketch, "E23.31.7", {"position": v(170.04, -18.85) * mm});
            skPoint(sketch, "E23.31.8", {"position": v(169, -25.9) * mm});
            skLineSegment(sketch, "E23.31.9", {"start": v(163.71, -21.38) * mm, "end": v(163, -26.33) * mm});
            skArc(sketch, "E23.31.10", {"start": v(163, -26.33) * mm, "mid": v(163.18, -27.07) * mm, "end": v(163.84, -27.46) * mm});
            skArc(sketch, "E23.31.11", {"start": v(164.85, -20.53) * mm, "mid": v(164.1, -20.72) * mm, "end": v(163.71, -21.38) * mm});
            skPoint(sketch, "E23.32.0", {"position": v(164.6, -13.89) * mm});
            skLineSegment(sketch, "E23.32.1", {"start": v(170.87, -12.77) * mm, "end": v(165.72, -11.52) * mm});
            skPoint(sketch, "E23.32.2", {"position": v(164.95, -6.78) * mm});
            skArc(sketch, "E23.32.3", {"start": v(171.8, -2.62) * mm, "mid": v(171.67, -3.25) * mm, "end": v(171.3, -3.78) * mm});
            skArc(sketch, "E23.32.4", {"start": v(171.25, -13.97) * mm, "mid": v(171.18, -13.33) * mm, "end": v(170.87, -12.77) * mm});
            skPoint(sketch, "E23.32.5", {"position": v(167.83, -8.12) * mm});
            skLineSegment(sketch, "E23.32.6", {"start": v(171.3, -3.78) * mm, "end": v(166.06, -4.53) * mm});
            skPoint(sketch, "E23.32.7", {"position": v(171.06, -2.35) * mm});
            skPoint(sketch, "E23.32.8", {"position": v(170.72, -9.46) * mm});
            skLineSegment(sketch, "E23.32.9", {"start": v(165.01, -5.48) * mm, "end": v(164.77, -10.47) * mm});
            skArc(sketch, "E23.32.10", {"start": v(164.77, -10.47) * mm, "mid": v(165.03, -11.2) * mm, "end": v(165.72, -11.52) * mm});
            skArc(sketch, "E23.32.11", {"start": v(166.06, -4.53) * mm, "mid": v(165.34, -4.79) * mm, "end": v(165.01, -5.48) * mm});
            skPoint(sketch, "E23.33.0", {"position": v(165.18, 2.07) * mm});
            skLineSegment(sketch, "E23.33.1", {"start": v(171.3, 3.78) * mm, "end": v(166.06, 4.53) * mm});
            skPoint(sketch, "E23.33.2", {"position": v(164.83, 9.18) * mm});
            skArc(sketch, "E23.33.3", {"start": v(171.25, 13.97) * mm, "mid": v(171.18, 13.33) * mm, "end": v(170.87, 12.77) * mm});
            skArc(sketch, "E23.33.4", {"start": v(171.8, 2.62) * mm, "mid": v(171.67, 3.25) * mm, "end": v(171.3, 3.78) * mm});
            skPoint(sketch, "E23.33.5", {"position": v(167.83, 8.12) * mm});
            skLineSegment(sketch, "E23.33.6", {"start": v(170.87, 12.77) * mm, "end": v(165.72, 11.52) * mm});
            skPoint(sketch, "E23.33.7", {"position": v(170.49, 14.17) * mm});
            skPoint(sketch, "E23.33.8", {"position": v(170.83, 7.06) * mm});
            skLineSegment(sketch, "E23.33.9", {"start": v(164.77, 10.47) * mm, "end": v(165.01, 5.48) * mm});
            skArc(sketch, "E23.33.10", {"start": v(165.01, 5.48) * mm, "mid": v(165.34, 4.79) * mm, "end": v(166.06, 4.53) * mm});
            skArc(sketch, "E23.33.11", {"start": v(165.72, 11.52) * mm, "mid": v(165.03, 11.2) * mm, "end": v(164.77, 10.47) * mm});
            skPoint(sketch, "E23.34.0", {"position": v(164.2, 18) * mm});
            skLineSegment(sketch, "E23.34.1", {"start": v(170.14, 20.3) * mm, "end": v(164.85, 20.53) * mm});
            skPoint(sketch, "E23.34.2", {"position": v(163.18, 25.04) * mm});
            skArc(sketch, "E23.34.3", {"start": v(169.1, 30.43) * mm, "mid": v(169.1, 29.8) * mm, "end": v(168.84, 29.2) * mm});
            skArc(sketch, "E23.34.4", {"start": v(170.74, 19.2) * mm, "mid": v(170.55, 19.8) * mm, "end": v(170.14, 20.3) * mm});
            skPoint(sketch, "E23.34.5", {"position": v(166.27, 24.28) * mm});
            skLineSegment(sketch, "E23.34.6", {"start": v(168.84, 29.2) * mm, "end": v(163.84, 27.46) * mm});
            skPoint(sketch, "E23.34.7", {"position": v(168.33, 30.56) * mm});
            skPoint(sketch, "E23.34.8", {"position": v(169.35, 23.51) * mm});
            skLineSegment(sketch, "E23.34.9", {"start": v(163, 26.33) * mm, "end": v(163.71, 21.38) * mm});
            skArc(sketch, "E23.34.10", {"start": v(163.71, 21.38) * mm, "mid": v(164.1, 20.72) * mm, "end": v(164.85, 20.53) * mm});
            skArc(sketch, "E23.34.11", {"start": v(163.84, 27.46) * mm, "mid": v(163.18, 27.07) * mm, "end": v(163, 26.33) * mm});
            skPoint(sketch, "E23.35.0", {"position": v(161.7, 33.76) * mm});
            skLineSegment(sketch, "E23.35.1", {"start": v(167.39, 36.62) * mm, "end": v(162.1, 36.35) * mm});
            skPoint(sketch, "E23.35.2", {"position": v(160, 40.67) * mm});
            skArc(sketch, "E23.35.3", {"start": v(165.38, 46.61) * mm, "mid": v(165.43, 45.97) * mm, "end": v(165.23, 45.36) * mm});
            skArc(sketch, "E23.35.4", {"start": v(168.1, 35.58) * mm, "mid": v(167.84, 36.17) * mm, "end": v(167.39, 36.62) * mm});
            skPoint(sketch, "E23.35.5", {"position": v(163.15, 40.21) * mm});
            skLineSegment(sketch, "E23.35.6", {"start": v(165.23, 45.36) * mm, "end": v(160.42, 43.14) * mm});
            skPoint(sketch, "E23.35.7", {"position": v(164.6, 46.66) * mm});
            skPoint(sketch, "E23.35.8", {"position": v(166.3, 39.75) * mm});
            skLineSegment(sketch, "E23.35.9", {"start": v(159.69, 41.93) * mm, "end": v(160.89, 37.08) * mm});
            skArc(sketch, "E23.35.10", {"start": v(160.89, 37.08) * mm, "mid": v(161.34, 36.46) * mm, "end": v(162.1, 36.35) * mm});
            skArc(sketch, "E23.35.11", {"start": v(160.42, 43.14) * mm, "mid": v(159.8, 42.7) * mm, "end": v(159.69, 41.93) * mm});
            skPoint(sketch, "E23.36.0", {"position": v(157.7, 49.21) * mm});
            skLineSegment(sketch, "E23.36.1", {"start": v(163.07, 52.6) * mm, "end": v(157.83, 51.82) * mm});
            skPoint(sketch, "E23.36.2", {"position": v(155.33, 55.93) * mm});
            skArc(sketch, "E23.36.3", {"start": v(160.1, 62.36) * mm, "mid": v(160.22, 61.72) * mm, "end": v(160.09, 61.1) * mm});
            skArc(sketch, "E23.36.4", {"start": v(163.88, 51.64) * mm, "mid": v(163.57, 52.2) * mm, "end": v(163.07, 52.6) * mm});
            skPoint(sketch, "E23.36.5", {"position": v(158.5, 55.77) * mm});
            skLineSegment(sketch, "E23.36.6", {"start": v(160.09, 61.1) * mm, "end": v(155.5, 58.43) * mm});
            skPoint(sketch, "E23.36.7", {"position": v(159.32, 62.33) * mm});
            skPoint(sketch, "E23.36.8", {"position": v(161.68, 55.61) * mm});
            skLineSegment(sketch, "E23.36.9", {"start": v(154.9, 57.15) * mm, "end": v(156.56, 52.43) * mm});
            skArc(sketch, "E23.36.10", {"start": v(156.56, 52.43) * mm, "mid": v(157.07, 51.86) * mm, "end": v(157.83, 51.82) * mm});
            skArc(sketch, "E23.36.11", {"start": v(155.5, 58.43) * mm, "mid": v(154.94, 57.92) * mm, "end": v(154.9, 57.15) * mm});
            skPoint(sketch, "E23.37.0", {"position": v(152.2, 64.2) * mm});
            skLineSegment(sketch, "E23.37.1", {"start": v(157.23, 68.1) * mm, "end": v(152.1, 66.81) * mm});
            skPoint(sketch, "E23.37.2", {"position": v(149.2, 70.66) * mm});
            skArc(sketch, "E23.37.3", {"start": v(153.34, 77.52) * mm, "mid": v(153.51, 76.9) * mm, "end": v(153.44, 76.26) * mm});
            skArc(sketch, "E23.37.4", {"start": v(158.13, 67.21) * mm, "mid": v(157.77, 67.74) * mm, "end": v(157.23, 68.1) * mm});
            skPoint(sketch, "E23.37.5", {"position": v(152.38, 70.8) * mm});
            skLineSegment(sketch, "E23.37.6", {"start": v(153.44, 76.26) * mm, "end": v(149.14, 73.16) * mm});
            skPoint(sketch, "E23.37.7", {"position": v(152.56, 77.42) * mm});
            skPoint(sketch, "E23.37.8", {"position": v(155.56, 70.96) * mm});
            skLineSegment(sketch, "E23.37.9", {"start": v(148.66, 71.83) * mm, "end": v(150.76, 67.3) * mm});
            skArc(sketch, "E23.37.10", {"start": v(150.76, 67.3) * mm, "mid": v(151.33, 66.78) * mm, "end": v(152.1, 66.81) * mm});
            skArc(sketch, "E23.37.11", {"start": v(149.14, 73.16) * mm, "mid": v(148.62, 72.6) * mm, "end": v(148.66, 71.83) * mm});
            skPoint(sketch, "E23.38.0", {"position": v(145.3, 78.6) * mm});
            skLineSegment(sketch, "E23.38.1", {"start": v(149.93, 82.96) * mm, "end": v(144.93, 81.18) * mm});
            skPoint(sketch, "E23.38.2", {"position": v(141.69, 84.73) * mm});
            skArc(sketch, "E23.38.3", {"start": v(145.14, 91.95) * mm, "mid": v(145.37, 91.36) * mm, "end": v(145.36, 90.72) * mm});
            skArc(sketch, "E23.38.4", {"start": v(150.9, 82.16) * mm, "mid": v(150.5, 82.65) * mm, "end": v(149.93, 82.96) * mm});
            skPoint(sketch, "E23.38.5", {"position": v(144.84, 85.18) * mm});
            skLineSegment(sketch, "E23.38.6", {"start": v(145.36, 90.72) * mm, "end": v(141.39, 87.22) * mm});
            skPoint(sketch, "E23.38.7", {"position": v(144.38, 91.78) * mm});
            skPoint(sketch, "E23.38.8", {"position": v(147.98, 85.64) * mm});
            skLineSegment(sketch, "E23.38.9", {"start": v(141.03, 85.85) * mm, "end": v(143.57, 81.54) * mm});
            skArc(sketch, "E23.38.10", {"start": v(143.57, 81.54) * mm, "mid": v(144.18, 81.08) * mm, "end": v(144.93, 81.18) * mm});
            skArc(sketch, "E23.38.11", {"start": v(141.39, 87.22) * mm, "mid": v(140.92, 86.6) * mm, "end": v(141.03, 85.85) * mm});
            skPoint(sketch, "E23.39.0", {"position": v(137.03, 92.25) * mm});
            skLineSegment(sketch, "E23.39.1", {"start": v(141.22, 97.04) * mm, "end": v(136.42, 94.8) * mm});
            skPoint(sketch, "E23.39.2", {"position": v(132.85, 98) * mm});
            skArc(sketch, "E23.39.3", {"start": v(135.59, 105.53) * mm, "mid": v(135.88, 104.96) * mm, "end": v(135.93, 104.32) * mm});
            skArc(sketch, "E23.39.4", {"start": v(142.27, 96.34) * mm, "mid": v(141.81, 96.8) * mm, "end": v(141.22, 97.04) * mm});
            skPoint(sketch, "E23.39.5", {"position": v(135.94, 98.77) * mm});
            skLineSegment(sketch, "E23.39.6", {"start": v(135.93, 104.32) * mm, "end": v(132.3, 100.45) * mm});
            skPoint(sketch, "E23.39.7", {"position": v(134.84, 105.28) * mm});
            skPoint(sketch, "E23.39.8", {"position": v(139.03, 99.52) * mm});
            skLineSegment(sketch, "E23.39.9", {"start": v(132.09, 99.06) * mm, "end": v(135.03, 95.01) * mm});
            skArc(sketch, "E23.39.10", {"start": v(135.03, 95.01) * mm, "mid": v(135.68, 94.61) * mm, "end": v(136.42, 94.8) * mm});
            skArc(sketch, "E23.39.11", {"start": v(132.3, 100.45) * mm, "mid": v(131.9, 99.8) * mm, "end": v(132.09, 99.06) * mm});
            skPoint(sketch, "E23.40.0", {"position": v(127.5, 105.04) * mm});
            skLineSegment(sketch, "E23.40.1", {"start": v(131.2, 110.22) * mm, "end": v(126.64, 107.51) * mm});
            skPoint(sketch, "E23.40.2", {"position": v(122.77, 110.37) * mm});
            skArc(sketch, "E23.40.3", {"start": v(124.77, 118.13) * mm, "mid": v(125.11, 117.59) * mm, "end": v(125.23, 116.95) * mm});
            skArc(sketch, "E23.40.4", {"start": v(132.3, 109.62) * mm, "mid": v(131.8, 110.03) * mm, "end": v(131.2, 110.22) * mm});
            skPoint(sketch, "E23.40.5", {"position": v(125.77, 111.42) * mm});
            skLineSegment(sketch, "E23.40.6", {"start": v(125.23, 116.95) * mm, "end": v(122, 112.75) * mm});
            skPoint(sketch, "E23.40.7", {"position": v(124.05, 117.8) * mm});
            skPoint(sketch, "E23.40.8", {"position": v(128.77, 112.48) * mm});
            skLineSegment(sketch, "E23.40.9", {"start": v(121.9, 111.34) * mm, "end": v(125.23, 107.6) * mm});
            skArc(sketch, "E23.40.10", {"start": v(125.23, 107.6) * mm, "mid": v(125.91, 107.26) * mm, "end": v(126.64, 107.51) * mm});
            skArc(sketch, "E23.40.11", {"start": v(122, 112.75) * mm, "mid": v(121.66, 112.07) * mm, "end": v(121.9, 111.34) * mm});
            skPoint(sketch, "E23.41.0", {"position": v(116.76, 116.86) * mm});
            skLineSegment(sketch, "E23.41.1", {"start": v(119.95, 122.36) * mm, "end": v(115.67, 119.23) * mm});
            skPoint(sketch, "E23.41.2", {"position": v(111.55, 121.7) * mm});
            skArc(sketch, "E23.41.3", {"start": v(112.79, 129.62) * mm, "mid": v(113.18, 129.11) * mm, "end": v(113.36, 128.5) * mm});
            skArc(sketch, "E23.41.4", {"start": v(121.1, 121.88) * mm, "mid": v(120.57, 122.24) * mm, "end": v(119.95, 122.36) * mm});
            skPoint(sketch, "E23.41.5", {"position": v(114.43, 123.04) * mm});
            skLineSegment(sketch, "E23.41.6", {"start": v(113.36, 128.5) * mm, "end": v(110.54, 124) * mm});
            skPoint(sketch, "E23.41.7", {"position": v(112.1, 129.23) * mm});
            skPoint(sketch, "E23.41.8", {"position": v(117.32, 124.38) * mm});
            skLineSegment(sketch, "E23.41.9", {"start": v(110.6, 122.59) * mm, "end": v(114.26, 119.18) * mm});
            skArc(sketch, "E23.41.10", {"start": v(114.26, 119.18) * mm, "mid": v(114.97, 118.92) * mm, "end": v(115.67, 119.23) * mm});
            skArc(sketch, "E23.41.11", {"start": v(110.54, 124) * mm, "mid": v(110.28, 123.28) * mm, "end": v(110.6, 122.59) * mm});
            skPoint(sketch, "E23.42.0", {"position": v(104.93, 127.58) * mm});
            skLineSegment(sketch, "E23.42.1", {"start": v(107.58, 133.37) * mm, "end": v(103.62, 129.84) * mm});
            skPoint(sketch, "E23.42.2", {"position": v(99.28, 131.9) * mm});
            skArc(sketch, "E23.42.3", {"start": v(99.75, 139.9) * mm, "mid": v(100.2, 139.43) * mm, "end": v(100.42, 138.83) * mm});
            skArc(sketch, "E23.42.4", {"start": v(108.78, 133) * mm, "mid": v(108.21, 133.3) * mm, "end": v(107.58, 133.37) * mm});
            skPoint(sketch, "E23.42.5", {"position": v(102.02, 133.51) * mm});
            skLineSegment(sketch, "E23.42.6", {"start": v(100.42, 138.83) * mm, "end": v(98.06, 134.1) * mm});
            skPoint(sketch, "E23.42.7", {"position": v(99.1, 139.45) * mm});
            skPoint(sketch, "E23.42.8", {"position": v(104.76, 135.12) * mm});
            skLineSegment(sketch, "E23.42.9", {"start": v(98.25, 132.7) * mm, "end": v(102.22, 129.65) * mm});
            skArc(sketch, "E23.42.10", {"start": v(102.22, 129.65) * mm, "mid": v(102.96, 129.46) * mm, "end": v(103.62, 129.84) * mm});
            skArc(sketch, "E23.42.11", {"start": v(98.06, 134.1) * mm, "mid": v(97.86, 133.35) * mm, "end": v(98.25, 132.7) * mm});
            skPoint(sketch, "E23.43.0", {"position": v(92.13, 137.11) * mm});
            skLineSegment(sketch, "E23.43.1", {"start": v(94.2, 143.13) * mm, "end": v(90.6, 139.24) * mm});
            skPoint(sketch, "E23.43.2", {"position": v(86.08, 140.87) * mm});
            skArc(sketch, "E23.43.3", {"start": v(85.78, 148.87) * mm, "mid": v(86.27, 148.45) * mm, "end": v(86.56, 147.88) * mm});
            skArc(sketch, "E23.43.4", {"start": v(95.44, 142.88) * mm, "mid": v(94.84, 143.12) * mm, "end": v(94.2, 143.13) * mm});
            skPoint(sketch, "E23.43.5", {"position": v(88.66, 142.74) * mm});
            skLineSegment(sketch, "E23.43.6", {"start": v(86.56, 147.88) * mm, "end": v(84.66, 142.93) * mm});
            skPoint(sketch, "E23.43.7", {"position": v(85.19, 148.36) * mm});
            skPoint(sketch, "E23.43.8", {"position": v(91.23, 144.6) * mm});
            skLineSegment(sketch, "E23.43.9", {"start": v(84.98, 141.55) * mm, "end": v(89.23, 138.91) * mm});
            skArc(sketch, "E23.43.10", {"start": v(89.23, 138.91) * mm, "mid": v(89.98, 138.8) * mm, "end": v(90.6, 139.24) * mm});
            skArc(sketch, "E23.43.11", {"start": v(84.66, 142.93) * mm, "mid": v(84.54, 142.17) * mm, "end": v(84.98, 141.55) * mm});
            skPoint(sketch, "E23.44.0", {"position": v(78.47, 145.36) * mm});
            skLineSegment(sketch, "E23.44.1", {"start": v(79.95, 151.55) * mm, "end": v(76.74, 147.33) * mm});
            skPoint(sketch, "E23.44.2", {"position": v(72.09, 148.52) * mm});
            skArc(sketch, "E23.44.3", {"start": v(71.01, 156.46) * mm, "mid": v(71.54, 156.08) * mm, "end": v(71.88, 155.54) * mm});
            skArc(sketch, "E23.44.4", {"start": v(81.2, 151.42) * mm, "mid": v(80.59, 151.6) * mm, "end": v(79.95, 151.55) * mm});
            skPoint(sketch, "E23.44.5", {"position": v(74.47, 150.63) * mm});
            skLineSegment(sketch, "E23.44.6", {"start": v(71.88, 155.54) * mm, "end": v(70.47, 150.43) * mm});
            skPoint(sketch, "E23.44.7", {"position": v(70.47, 155.89) * mm});
            skPoint(sketch, "E23.44.8", {"position": v(76.85, 152.73) * mm});
            skLineSegment(sketch, "E23.44.9", {"start": v(70.92, 149.1) * mm, "end": v(75.4, 146.88) * mm});
            skArc(sketch, "E23.44.10", {"start": v(75.4, 146.88) * mm, "mid": v(76.17, 146.83) * mm, "end": v(76.74, 147.33) * mm});
            skArc(sketch, "E23.44.11", {"start": v(70.47, 150.43) * mm, "mid": v(70.42, 149.67) * mm, "end": v(70.92, 149.1) * mm});
            skPoint(sketch, "E23.45.0", {"position": v(64.07, 152.26) * mm});
            skLineSegment(sketch, "E23.45.1", {"start": v(64.95, 158.56) * mm, "end": v(62.17, 154.05) * mm});
            skPoint(sketch, "E23.45.2", {"position": v(57.42, 154.78) * mm});
            skArc(sketch, "E23.45.3", {"start": v(55.58, 162.58) * mm, "mid": v(56.14, 162.26) * mm, "end": v(56.53, 161.75) * mm});
            skArc(sketch, "E23.45.4", {"start": v(66.2, 158.55) * mm, "mid": v(65.58, 158.68) * mm, "end": v(64.95, 158.56) * mm});
            skPoint(sketch, "E23.45.5", {"position": v(59.58, 157.11) * mm});
            skLineSegment(sketch, "E23.45.6", {"start": v(56.53, 161.75) * mm, "end": v(55.62, 156.53) * mm});
            skPoint(sketch, "E23.45.7", {"position": v(55.1, 161.96) * mm});
            skPoint(sketch, "E23.45.8", {"position": v(61.75, 159.44) * mm});
            skLineSegment(sketch, "E23.45.9", {"start": v(56.2, 155.24) * mm, "end": v(60.88, 153.47) * mm});
            skArc(sketch, "E23.45.10", {"start": v(60.88, 153.47) * mm, "mid": v(61.64, 153.5) * mm, "end": v(62.17, 154.05) * mm});
            skArc(sketch, "E23.45.11", {"start": v(55.62, 156.53) * mm, "mid": v(55.64, 155.77) * mm, "end": v(56.2, 155.24) * mm});
            skPoint(sketch, "E23.46.0", {"position": v(49.08, 157.73) * mm});
            skLineSegment(sketch, "E23.46.1", {"start": v(49.34, 164.1) * mm, "end": v(47, 159.33) * mm});
            skPoint(sketch, "E23.46.2", {"position": v(42.2, 159.6) * mm});
            skArc(sketch, "E23.46.3", {"start": v(39.63, 167.19) * mm, "mid": v(40.22, 166.92) * mm, "end": v(40.66, 166.45) * mm});
            skArc(sketch, "E23.46.4", {"start": v(50.6, 164.2) * mm, "mid": v(49.96, 164.27) * mm, "end": v(49.34, 164.1) * mm});
            skPoint(sketch, "E23.46.5", {"position": v(44.14, 162.13) * mm});
            skLineSegment(sketch, "E23.46.6", {"start": v(40.66, 166.45) * mm, "end": v(40.25, 161.17) * mm});
            skPoint(sketch, "E23.46.7", {"position": v(39.2, 166.52) * mm});
            skPoint(sketch, "E23.46.8", {"position": v(46.08, 164.65) * mm});
            skLineSegment(sketch, "E23.46.9", {"start": v(40.96, 159.94) * mm, "end": v(45.78, 158.63) * mm});
            skArc(sketch, "E23.46.10", {"start": v(45.78, 158.63) * mm, "mid": v(46.54, 158.73) * mm, "end": v(47, 159.33) * mm});
            skArc(sketch, "E23.46.11", {"start": v(40.25, 161.17) * mm, "mid": v(40.35, 160.41) * mm, "end": v(40.96, 159.94) * mm});
            skPoint(sketch, "E23.47.0", {"position": v(33.63, 161.73) * mm});
            skLineSegment(sketch, "E23.47.1", {"start": v(33.27, 168.09) * mm, "end": v(31.41, 163.12) * mm});
            skPoint(sketch, "E23.47.2", {"position": v(26.6, 162.93) * mm});
            skArc(sketch, "E23.47.3", {"start": v(23.31, 170.23) * mm, "mid": v(23.92, 170.02) * mm, "end": v(24.4, 169.6) * mm});
            skArc(sketch, "E23.47.4", {"start": v(34.51, 168.32) * mm, "mid": v(33.87, 168.32) * mm, "end": v(33.27, 168.09) * mm});
            skPoint(sketch, "E23.47.5", {"position": v(28.29, 165.63) * mm});
            skLineSegment(sketch, "E23.47.6", {"start": v(24.4, 169.6) * mm, "end": v(24.51, 164.3) * mm});
            skPoint(sketch, "E23.47.7", {"position": v(22.95, 169.53) * mm});
            skPoint(sketch, "E23.47.8", {"position": v(29.97, 168.33) * mm});
            skLineSegment(sketch, "E23.47.9", {"start": v(25.33, 163.15) * mm, "end": v(30.26, 162.3) * mm});
            skArc(sketch, "E23.47.10", {"start": v(30.26, 162.3) * mm, "mid": v(31, 162.48) * mm, "end": v(31.41, 163.12) * mm});
            skArc(sketch, "E23.47.11", {"start": v(24.51, 164.3) * mm, "mid": v(24.68, 163.56) * mm, "end": v(25.33, 163.15) * mm});
            skPoint(sketch, "E23.48.0", {"position": v(17.86, 164.22) * mm});
            skLineSegment(sketch, "E23.48.1", {"start": v(16.9, 170.51) * mm, "end": v(15.52, 165.4) * mm});
            skPoint(sketch, "E23.48.2", {"position": v(10.76, 164.74) * mm});
            skArc(sketch, "E23.48.3", {"start": v(6.77, 171.69) * mm, "mid": v(7.4, 171.54) * mm, "end": v(7.92, 171.16) * mm});
            skArc(sketch, "E23.48.4", {"start": v(18.1, 170.86) * mm, "mid": v(17.47, 170.8) * mm, "end": v(16.9, 170.51) * mm});
            skPoint(sketch, "E23.48.5", {"position": v(12.17, 167.59) * mm});
            skLineSegment(sketch, "E23.48.6", {"start": v(7.92, 171.16) * mm, "end": v(8.54, 165.9) * mm});
            skPoint(sketch, "E23.48.7", {"position": v(6.48, 170.95) * mm});
            skPoint(sketch, "E23.48.8", {"position": v(13.58, 170.44) * mm});
            skLineSegment(sketch, "E23.48.9", {"start": v(9.46, 164.83) * mm, "end": v(14.45, 164.47) * mm});
            skArc(sketch, "E23.48.10", {"start": v(14.45, 164.47) * mm, "mid": v(15.18, 164.71) * mm, "end": v(15.52, 165.4) * mm});
            skArc(sketch, "E23.48.11", {"start": v(8.54, 165.9) * mm, "mid": v(8.78, 165.18) * mm, "end": v(9.46, 164.83) * mm});
            skPoint(sketch, "E23.49.0", {"position": v(1.93, 165.18) * mm});
            skLineSegment(sketch, "E23.49.1", {"start": v(0.36, 171.35) * mm, "end": v(-0.51, 166.12) * mm});
            skPoint(sketch, "E23.49.2", {"position": v(-5.2, 165) * mm});
            skArc(sketch, "E23.49.3", {"start": v(-9.83, 171.54) * mm, "mid": v(-9.2, 171.45) * mm, "end": v(-8.64, 171.13) * mm});
            skArc(sketch, "E23.49.4", {"start": v(1.53, 171.81) * mm, "mid": v(0.9, 171.7) * mm, "end": v(0.36, 171.35) * mm});
            skPoint(sketch, "E23.49.5", {"position": v(-4.06, 167.98) * mm});
            skLineSegment(sketch, "E23.49.6", {"start": v(-8.64, 171.13) * mm, "end": v(-7.51, 165.95) * mm});
            skPoint(sketch, "E23.49.7", {"position": v(-10.05, 170.78) * mm});
            skPoint(sketch, "E23.49.8", {"position": v(-2.93, 170.95) * mm});
            skLineSegment(sketch, "E23.49.9", {"start": v(-6.49, 164.98) * mm, "end": v(-1.49, 165.1) * mm});
            skArc(sketch, "E23.49.10", {"start": v(-1.49, 165.1) * mm, "mid": v(-0.79, 165.4) * mm, "end": v(-0.51, 166.12) * mm});
            skArc(sketch, "E23.49.11", {"start": v(-7.51, 165.95) * mm, "mid": v(-7.2, 165.25) * mm, "end": v(-6.49, 164.98) * mm});
            skPoint(sketch, "E23.50.0", {"position": v(-14.02, 164.6) * mm});
            skLineSegment(sketch, "E23.50.1", {"start": v(-16.18, 170.58) * mm, "end": v(-16.54, 165.3) * mm});
            skPoint(sketch, "E23.50.2", {"position": v(-21.1, 163.74) * mm});
            skArc(sketch, "E23.50.3", {"start": v(-26.34, 169.79) * mm, "mid": v(-25.7, 169.76) * mm, "end": v(-25.11, 169.5) * mm});
            skArc(sketch, "E23.50.4", {"start": v(-15.06, 171.16) * mm, "mid": v(-15.68, 170.98) * mm, "end": v(-16.18, 170.58) * mm});
            skPoint(sketch, "E23.50.5", {"position": v(-20.25, 166.8) * mm});
            skLineSegment(sketch, "E23.50.6", {"start": v(-25.11, 169.5) * mm, "end": v(-23.5, 164.45) * mm});
            skPoint(sketch, "E23.50.7", {"position": v(-26.48, 169.02) * mm});
            skPoint(sketch, "E23.50.8", {"position": v(-19.42, 169.87) * mm});
            skLineSegment(sketch, "E23.50.9", {"start": v(-22.38, 163.58) * mm, "end": v(-17.42, 164.18) * mm});
            skArc(sketch, "E23.50.10", {"start": v(-17.42, 164.18) * mm, "mid": v(-16.75, 164.56) * mm, "end": v(-16.54, 165.3) * mm});
            skArc(sketch, "E23.50.11", {"start": v(-23.5, 164.45) * mm, "mid": v(-23.12, 163.78) * mm, "end": v(-22.38, 163.58) * mm});
            skPoint(sketch, "E23.51.0", {"position": v(-29.84, 162.47) * mm});
            skLineSegment(sketch, "E23.51.1", {"start": v(-32.57, 168.22) * mm, "end": v(-32.42, 162.93) * mm});
            skPoint(sketch, "E23.51.2", {"position": v(-36.8, 160.94) * mm});
            skArc(sketch, "E23.51.3", {"start": v(-42.6, 166.45) * mm, "mid": v(-41.96, 166.5) * mm, "end": v(-41.36, 166.28) * mm});
            skArc(sketch, "E23.51.4", {"start": v(-31.5, 168.9) * mm, "mid": v(-32.1, 168.67) * mm, "end": v(-32.57, 168.22) * mm});
            skPoint(sketch, "E23.51.5", {"position": v(-36.26, 164.07) * mm});
            skLineSegment(sketch, "E23.51.6", {"start": v(-41.36, 166.28) * mm, "end": v(-39.26, 161.42) * mm});
            skPoint(sketch, "E23.51.7", {"position": v(-42.67, 165.67) * mm});
            skPoint(sketch, "E23.51.8", {"position": v(-35.72, 167.2) * mm});
            skLineSegment(sketch, "E23.51.9", {"start": v(-38.06, 160.66) * mm, "end": v(-33.18, 161.73) * mm});
            skArc(sketch, "E23.51.10", {"start": v(-33.18, 161.73) * mm, "mid": v(-32.55, 162.17) * mm, "end": v(-32.42, 162.93) * mm});
            skArc(sketch, "E23.51.11", {"start": v(-39.26, 161.42) * mm, "mid": v(-38.82, 160.79) * mm, "end": v(-38.06, 160.66) * mm});
            skPoint(sketch, "E23.52.0", {"position": v(-45.39, 158.83) * mm});
            skLineSegment(sketch, "E23.52.1", {"start": v(-48.65, 164.3) * mm, "end": v(-48, 159.04) * mm});
            skPoint(sketch, "E23.52.2", {"position": v(-52.16, 156.63) * mm});
            skArc(sketch, "E23.52.3", {"start": v(-58.47, 161.56) * mm, "mid": v(-57.84, 161.66) * mm, "end": v(-57.21, 161.51) * mm});
            skArc(sketch, "E23.52.4", {"start": v(-47.66, 165.08) * mm, "mid": v(-48.23, 164.78) * mm, "end": v(-48.65, 164.3) * mm});
            skPoint(sketch, "E23.52.5", {"position": v(-51.92, 159.8) * mm});
            skLineSegment(sketch, "E23.52.6", {"start": v(-57.21, 161.51) * mm, "end": v(-54.65, 156.87) * mm});
            skPoint(sketch, "E23.52.7", {"position": v(-58.46, 160.78) * mm});
            skPoint(sketch, "E23.52.8", {"position": v(-51.7, 162.98) * mm});
            skLineSegment(sketch, "E23.52.9", {"start": v(-53.4, 156.23) * mm, "end": v(-48.64, 157.78) * mm});
            skArc(sketch, "E23.52.10", {"start": v(-48.64, 157.78) * mm, "mid": v(-48.05, 158.27) * mm, "end": v(-48, 159.04) * mm});
            skArc(sketch, "E23.52.11", {"start": v(-54.65, 156.87) * mm, "mid": v(-54.15, 156.3) * mm, "end": v(-53.4, 156.23) * mm});
            skPoint(sketch, "E23.53.0", {"position": v(-60.5, 153.71) * mm});
            skLineSegment(sketch, "E23.53.1", {"start": v(-64.28, 158.83) * mm, "end": v(-63.12, 153.66) * mm});
            skPoint(sketch, "E23.53.2", {"position": v(-67.03, 150.87) * mm});
            skArc(sketch, "E23.53.3", {"start": v(-73.79, 155.17) * mm, "mid": v(-73.17, 155.33) * mm, "end": v(-72.53, 155.24) * mm});
            skArc(sketch, "E23.53.4", {"start": v(-63.37, 159.7) * mm, "mid": v(-63.91, 159.36) * mm, "end": v(-64.28, 158.83) * mm});
            skPoint(sketch, "E23.53.5", {"position": v(-67.1, 154.05) * mm});
            skLineSegment(sketch, "E23.53.6", {"start": v(-72.53, 155.24) * mm, "end": v(-69.54, 150.87) * mm});
            skPoint(sketch, "E23.53.7", {"position": v(-73.7, 154.39) * mm});
            skPoint(sketch, "E23.53.8", {"position": v(-67.18, 157.23) * mm});
            skLineSegment(sketch, "E23.53.9", {"start": v(-68.22, 150.35) * mm, "end": v(-63.64, 152.35) * mm});
            skArc(sketch, "E23.53.10", {"start": v(-63.64, 152.35) * mm, "mid": v(-63.1, 152.9) * mm, "end": v(-63.12, 153.66) * mm});
            skArc(sketch, "E23.53.11", {"start": v(-69.54, 150.87) * mm, "mid": v(-68.99, 150.34) * mm, "end": v(-68.22, 150.35) * mm});
            skPoint(sketch, "E23.54.0", {"position": v(-75.06, 147.15) * mm});
            skLineSegment(sketch, "E23.54.1", {"start": v(-79.31, 151.89) * mm, "end": v(-77.66, 146.85) * mm});
            skPoint(sketch, "E23.54.2", {"position": v(-81.28, 143.7) * mm});
            skArc(sketch, "E23.54.3", {"start": v(-88.42, 147.32) * mm, "mid": v(-87.82, 147.54) * mm, "end": v(-87.18, 147.51) * mm});
            skArc(sketch, "E23.54.4", {"start": v(-78.5, 152.84) * mm, "mid": v(-79, 152.45) * mm, "end": v(-79.31, 151.89) * mm});
            skPoint(sketch, "E23.54.5", {"position": v(-81.66, 146.85) * mm});
            skLineSegment(sketch, "E23.54.6", {"start": v(-87.18, 147.51) * mm, "end": v(-83.77, 143.45) * mm});
            skPoint(sketch, "E23.54.7", {"position": v(-88.26, 146.55) * mm});
            skPoint(sketch, "E23.54.8", {"position": v(-82.04, 150.01) * mm});
            skLineSegment(sketch, "E23.54.9", {"start": v(-82.41, 143.06) * mm, "end": v(-78.04, 145.5) * mm});
            skArc(sketch, "E23.54.10", {"start": v(-78.04, 145.5) * mm, "mid": v(-77.57, 146.1) * mm, "end": v(-77.66, 146.85) * mm});
            skArc(sketch, "E23.54.11", {"start": v(-83.77, 143.45) * mm, "mid": v(-83.17, 142.98) * mm, "end": v(-82.41, 143.06) * mm});
            skPoint(sketch, "E23.55.0", {"position": v(-88.9, 139.22) * mm});
            skLineSegment(sketch, "E23.55.1", {"start": v(-93.6, 143.52) * mm, "end": v(-91.47, 138.67) * mm});
            skPoint(sketch, "E23.55.2", {"position": v(-94.77, 135.18) * mm});
            skArc(sketch, "E23.55.3", {"start": v(-102.23, 138.1) * mm, "mid": v(-101.65, 138.38) * mm, "end": v(-101, 138.41) * mm});
            skArc(sketch, "E23.55.4", {"start": v(-92.88, 144.55) * mm, "mid": v(-93.34, 144.11) * mm, "end": v(-93.6, 143.52) * mm});
            skPoint(sketch, "E23.55.5", {"position": v(-95.45, 138.29) * mm});
            skLineSegment(sketch, "E23.55.6", {"start": v(-101, 138.41) * mm, "end": v(-97.23, 134.7) * mm});
            skPoint(sketch, "E23.55.7", {"position": v(-102, 137.35) * mm});
            skPoint(sketch, "E23.55.8", {"position": v(-96.14, 141.4) * mm});
            skLineSegment(sketch, "E23.55.9", {"start": v(-95.84, 134.44) * mm, "end": v(-91.72, 137.28) * mm});
            skArc(sketch, "E23.55.10", {"start": v(-91.72, 137.28) * mm, "mid": v(-91.3, 137.92) * mm, "end": v(-91.47, 138.67) * mm});
            skArc(sketch, "E23.55.11", {"start": v(-97.23, 134.7) * mm, "mid": v(-96.58, 134.28) * mm, "end": v(-95.84, 134.44) * mm});
            skPoint(sketch, "E23.56.0", {"position": v(-101.93, 130) * mm});
            skLineSegment(sketch, "E23.56.1", {"start": v(-107.01, 133.82) * mm, "end": v(-104.42, 129.2) * mm});
            skPoint(sketch, "E23.56.2", {"position": v(-107.37, 125.4) * mm});
            skArc(sketch, "E23.56.3", {"start": v(-115.08, 127.59) * mm, "mid": v(-114.53, 127.92) * mm, "end": v(-113.9, 128.02) * mm});
            skArc(sketch, "E23.56.4", {"start": v(-106.4, 134.92) * mm, "mid": v(-106.81, 134.43) * mm, "end": v(-107.01, 133.82) * mm});
            skPoint(sketch, "E23.56.5", {"position": v(-108.35, 128.43) * mm});
            skLineSegment(sketch, "E23.56.6", {"start": v(-113.9, 128.02) * mm, "end": v(-109.77, 124.68) * mm});
            skPoint(sketch, "E23.56.7", {"position": v(-114.77, 126.86) * mm});
            skPoint(sketch, "E23.56.8", {"position": v(-109.33, 131.45) * mm});
            skLineSegment(sketch, "E23.56.9", {"start": v(-108.36, 124.56) * mm, "end": v(-104.54, 127.79) * mm});
            skArc(sketch, "E23.56.10", {"start": v(-104.54, 127.79) * mm, "mid": v(-104.2, 128.47) * mm, "end": v(-104.42, 129.2) * mm});
            skArc(sketch, "E23.56.11", {"start": v(-109.77, 124.68) * mm, "mid": v(-109.1, 124.33) * mm, "end": v(-108.36, 124.56) * mm});
            skPoint(sketch, "E23.57.0", {"position": v(-114, 119.55) * mm});
            skLineSegment(sketch, "E23.57.1", {"start": v(-119.43, 122.87) * mm, "end": v(-116.4, 118.52) * mm});
            skPoint(sketch, "E23.57.2", {"position": v(-118.97, 114.45) * mm});
            skArc(sketch, "E23.57.3", {"start": v(-126.85, 115.89) * mm, "mid": v(-126.34, 116.27) * mm, "end": v(-125.72, 116.43) * mm});
            skArc(sketch, "E23.57.4", {"start": v(-118.92, 124.02) * mm, "mid": v(-119.29, 123.5) * mm, "end": v(-119.43, 122.87) * mm});
            skPoint(sketch, "E23.57.5", {"position": v(-120.24, 117.37) * mm});
            skLineSegment(sketch, "E23.57.6", {"start": v(-125.72, 116.43) * mm, "end": v(-121.3, 113.5) * mm});
            skPoint(sketch, "E23.57.7", {"position": v(-126.48, 115.2) * mm});
            skPoint(sketch, "E23.57.8", {"position": v(-121.51, 120.29) * mm});
            skLineSegment(sketch, "E23.57.9", {"start": v(-119.88, 113.52) * mm, "end": v(-116.39, 117.1) * mm});
            skArc(sketch, "E23.57.10", {"start": v(-116.39, 117.1) * mm, "mid": v(-116.1, 117.81) * mm, "end": v(-116.4, 118.52) * mm});
            skArc(sketch, "E23.57.11", {"start": v(-121.3, 113.5) * mm, "mid": v(-120.58, 113.22) * mm, "end": v(-119.88, 113.52) * mm});
            skPoint(sketch, "E23.58.0", {"position": v(-125, 107.99) * mm});
            skLineSegment(sketch, "E23.58.1", {"start": v(-130.73, 110.77) * mm, "end": v(-127.3, 106.73) * mm});
            skPoint(sketch, "E23.58.2", {"position": v(-129.46, 102.44) * mm});
            skArc(sketch, "E23.58.3", {"start": v(-137.45, 103.1) * mm, "mid": v(-136.97, 103.53) * mm, "end": v(-136.37, 103.75) * mm});
            skArc(sketch, "E23.58.4", {"start": v(-130.33, 111.96) * mm, "mid": v(-130.65, 111.4) * mm, "end": v(-130.73, 110.77) * mm});
            skPoint(sketch, "E23.58.5", {"position": v(-131, 105.22) * mm});
            skLineSegment(sketch, "E23.58.6", {"start": v(-136.37, 103.75) * mm, "end": v(-131.68, 101.27) * mm});
            skPoint(sketch, "E23.58.7", {"position": v(-137.01, 102.45) * mm});
            skPoint(sketch, "E23.58.8", {"position": v(-132.55, 108) * mm});
            skLineSegment(sketch, "E23.58.9", {"start": v(-130.28, 101.42) * mm, "end": v(-127.15, 105.32) * mm});
            skArc(sketch, "E23.58.10", {"start": v(-127.15, 105.32) * mm, "mid": v(-126.93, 106.06) * mm, "end": v(-127.3, 106.73) * mm});
            skArc(sketch, "E23.58.11", {"start": v(-131.68, 101.27) * mm, "mid": v(-130.95, 101.06) * mm, "end": v(-130.28, 101.42) * mm});
            skPoint(sketch, "E23.59.0", {"position": v(-134.85, 95.42) * mm});
            skLineSegment(sketch, "E23.59.1", {"start": v(-140.81, 97.63) * mm, "end": v(-137, 93.94) * mm});
            skPoint(sketch, "E23.59.2", {"position": v(-138.75, 89.46) * mm});
            skArc(sketch, "E23.59.3", {"start": v(-146.76, 89.36) * mm, "mid": v(-146.32, 89.83) * mm, "end": v(-145.74, 90.1) * mm});
            skArc(sketch, "E23.59.4", {"start": v(-140.53, 98.86) * mm, "mid": v(-140.8, 98.27) * mm, "end": v(-140.81, 97.63) * mm});
            skPoint(sketch, "E23.59.5", {"position": v(-140.55, 92.08) * mm});
            skLineSegment(sketch, "E23.59.6", {"start": v(-145.74, 90.1) * mm, "end": v(-140.84, 88.09) * mm});
            skPoint(sketch, "E23.59.7", {"position": v(-146.26, 88.75) * mm});
            skPoint(sketch, "E23.59.8", {"position": v(-142.36, 94.7) * mm});
            skLineSegment(sketch, "E23.59.9", {"start": v(-139.46, 88.38) * mm, "end": v(-136.72, 92.56) * mm});
            skArc(sketch, "E23.59.10", {"start": v(-136.72, 92.56) * mm, "mid": v(-136.58, 93.31) * mm, "end": v(-137, 93.94) * mm});
            skArc(sketch, "E23.59.11", {"start": v(-140.84, 88.09) * mm, "mid": v(-140.1, 87.95) * mm, "end": v(-139.46, 88.38) * mm});
            skPoint(sketch, "E23.60.0", {"position": v(-143.43, 81.96) * mm});
            skLineSegment(sketch, "E23.60.1", {"start": v(-149.58, 83.59) * mm, "end": v(-145.43, 80.28) * mm});
            skPoint(sketch, "E23.60.2", {"position": v(-146.73, 75.65) * mm});
            skArc(sketch, "E23.60.3", {"start": v(-154.7, 74.77) * mm, "mid": v(-154.31, 75.29) * mm, "end": v(-153.76, 75.62) * mm});
            skArc(sketch, "E23.60.4", {"start": v(-149.41, 84.84) * mm, "mid": v(-149.62, 84.23) * mm, "end": v(-149.58, 83.59) * mm});
            skPoint(sketch, "E23.60.5", {"position": v(-148.78, 78.09) * mm});
            skLineSegment(sketch, "E23.60.6", {"start": v(-153.76, 75.62) * mm, "end": v(-148.69, 74.08) * mm});
            skPoint(sketch, "E23.60.7", {"position": v(-154.14, 74.22) * mm});
            skPoint(sketch, "E23.60.8", {"position": v(-150.83, 80.52) * mm});
            skLineSegment(sketch, "E23.60.9", {"start": v(-147.34, 74.5) * mm, "end": v(-145.01, 78.93) * mm});
            skArc(sketch, "E23.60.10", {"start": v(-145.01, 78.93) * mm, "mid": v(-144.94, 79.7) * mm, "end": v(-145.43, 80.28) * mm});
            skArc(sketch, "E23.60.11", {"start": v(-148.69, 74.08) * mm, "mid": v(-147.92, 74.01) * mm, "end": v(-147.34, 74.5) * mm});
            skPoint(sketch, "E23.61.0", {"position": v(-150.67, 67.73) * mm});
            skLineSegment(sketch, "E23.61.1", {"start": v(-156.95, 68.76) * mm, "end": v(-152.5, 65.87) * mm});
            skPoint(sketch, "E23.61.2", {"position": v(-153.35, 61.14) * mm});
            skArc(sketch, "E23.61.3", {"start": v(-161.19, 59.5) * mm, "mid": v(-160.86, 60.04) * mm, "end": v(-160.34, 60.42) * mm});
            skArc(sketch, "E23.61.4", {"start": v(-156.9, 70.02) * mm, "mid": v(-157.05, 69.4) * mm, "end": v(-156.95, 68.76) * mm});
            skPoint(sketch, "E23.61.5", {"position": v(-155.63, 63.36) * mm});
            skLineSegment(sketch, "E23.61.6", {"start": v(-160.34, 60.42) * mm, "end": v(-155.14, 59.39) * mm});
            skPoint(sketch, "E23.61.7", {"position": v(-160.58, 59) * mm});
            skPoint(sketch, "E23.61.8", {"position": v(-157.9, 65.59) * mm});
            skLineSegment(sketch, "E23.61.9", {"start": v(-153.84, 59.94) * mm, "end": v(-151.95, 64.57) * mm});
            skArc(sketch, "E23.61.10", {"start": v(-151.95, 64.57) * mm, "mid": v(-151.96, 65.33) * mm, "end": v(-152.5, 65.87) * mm});
            skArc(sketch, "E23.61.11", {"start": v(-155.14, 59.39) * mm, "mid": v(-154.38, 59.4) * mm, "end": v(-153.84, 59.94) * mm});
            skPoint(sketch, "E23.62.0", {"position": v(-156.5, 52.88) * mm});
            skLineSegment(sketch, "E23.62.1", {"start": v(-162.85, 53.3) * mm, "end": v(-158.15, 50.84) * mm});
            skPoint(sketch, "E23.62.2", {"position": v(-158.54, 46.05) * mm});
            skArc(sketch, "E23.62.3", {"start": v(-166.18, 43.66) * mm, "mid": v(-165.9, 44.24) * mm, "end": v(-165.42, 44.67) * mm});
            skArc(sketch, "E23.62.4", {"start": v(-162.93, 54.55) * mm, "mid": v(-163.01, 53.91) * mm, "end": v(-162.85, 53.3) * mm});
            skPoint(sketch, "E23.62.5", {"position": v(-161.01, 48.05) * mm});
            skLineSegment(sketch, "E23.62.6", {"start": v(-165.42, 44.67) * mm, "end": v(-160.15, 44.14) * mm});
            skPoint(sketch, "E23.62.7", {"position": v(-165.53, 43.22) * mm});
            skPoint(sketch, "E23.62.8", {"position": v(-163.5, 50.04) * mm});
            skLineSegment(sketch, "E23.62.9", {"start": v(-158.9, 44.8) * mm, "end": v(-157.48, 49.6) * mm});
            skArc(sketch, "E23.62.10", {"start": v(-157.48, 49.6) * mm, "mid": v(-157.56, 50.36) * mm, "end": v(-158.15, 50.84) * mm});
            skArc(sketch, "E23.62.11", {"start": v(-160.15, 44.14) * mm, "mid": v(-159.39, 44.22) * mm, "end": v(-158.9, 44.8) * mm});
            skPoint(sketch, "E23.63.0", {"position": v(-160.87, 37.52) * mm});
            skLineSegment(sketch, "E23.63.1", {"start": v(-167.23, 37.33) * mm, "end": v(-162.32, 35.34) * mm});
            skPoint(sketch, "E23.63.2", {"position": v(-162.24, 30.54) * mm});
            skArc(sketch, "E23.63.3", {"start": v(-169.62, 27.42) * mm, "mid": v(-169.4, 28.02) * mm, "end": v(-168.96, 28.5) * mm});
            skArc(sketch, "E23.63.4", {"start": v(-167.43, 38.57) * mm, "mid": v(-167.46, 37.93) * mm, "end": v(-167.23, 37.33) * mm});
            skPoint(sketch, "E23.63.5", {"position": v(-164.9, 32.28) * mm});
            skLineSegment(sketch, "E23.63.6", {"start": v(-168.96, 28.5) * mm, "end": v(-163.66, 28.47) * mm});
            skPoint(sketch, "E23.63.7", {"position": v(-168.93, 27.04) * mm});
            skPoint(sketch, "E23.63.8", {"position": v(-167.56, 34.03) * mm});
            skLineSegment(sketch, "E23.63.9", {"start": v(-162.49, 29.26) * mm, "end": v(-161.53, 34.17) * mm});
            skArc(sketch, "E23.63.10", {"start": v(-161.53, 34.17) * mm, "mid": v(-161.68, 34.92) * mm, "end": v(-162.32, 35.34) * mm});
            skArc(sketch, "E23.63.11", {"start": v(-163.66, 28.47) * mm, "mid": v(-162.91, 28.63) * mm, "end": v(-162.49, 29.26) * mm});
            skPoint(sketch, "E23.64.0", {"position": v(-163.74, 21.82) * mm});
            skLineSegment(sketch, "E23.64.1", {"start": v(-170.05, 21.01) * mm, "end": v(-164.97, 19.51) * mm});
            skPoint(sketch, "E23.64.2", {"position": v(-164.43, 14.74) * mm});
            skArc(sketch, "E23.64.3", {"start": v(-171.47, 10.92) * mm, "mid": v(-171.3, 11.54) * mm, "end": v(-170.92, 12.05) * mm});
            skArc(sketch, "E23.64.4", {"start": v(-170.37, 22.23) * mm, "mid": v(-170.33, 21.59) * mm, "end": v(-170.05, 21.01) * mm});
            skPoint(sketch, "E23.64.5", {"position": v(-167.25, 16.22) * mm});
            skLineSegment(sketch, "E23.64.6", {"start": v(-170.92, 12.05) * mm, "end": v(-165.65, 12.55) * mm});
            skPoint(sketch, "E23.64.7", {"position": v(-170.75, 10.61) * mm});
            skPoint(sketch, "E23.64.8", {"position": v(-170.06, 17.7) * mm});
            skLineSegment(sketch, "E23.64.9", {"start": v(-164.56, 13.44) * mm, "end": v(-164.07, 18.42) * mm});
            skArc(sketch, "E23.64.10", {"start": v(-164.07, 18.42) * mm, "mid": v(-164.3, 19.15) * mm, "end": v(-164.97, 19.51) * mm});
            skArc(sketch, "E23.64.11", {"start": v(-165.65, 12.55) * mm, "mid": v(-164.91, 12.77) * mm, "end": v(-164.56, 13.44) * mm});
            skArc(sketch, "E24.trimOffspring", {"start": v(-171.47, 10.92) * mm, "mid": v(-171.62, 8.3) * mm, "end": v(-171.72, 5.68) * mm});
            skArc(sketch, "E25.trimOffspring", {"start": v(-169.62, 27.42) * mm, "mid": v(-170.02, 24.83) * mm, "end": v(-170.37, 22.23) * mm});
            skArc(sketch, "E26.trimOffspring", {"start": v(-166.18, 43.66) * mm, "mid": v(-166.83, 41.12) * mm, "end": v(-167.43, 38.57) * mm});
            skArc(sketch, "E27.trimOffspring", {"start": v(-161.19, 59.5) * mm, "mid": v(-162.08, 57.03) * mm, "end": v(-162.93, 54.55) * mm});
            skArc(sketch, "E28.trimOffspring", {"start": v(-154.7, 74.77) * mm, "mid": v(-155.82, 72.4) * mm, "end": v(-156.9, 70.02) * mm});
            skArc(sketch, "E29.trimOffspring", {"start": v(-146.76, 89.36) * mm, "mid": v(-148.1, 87.1) * mm, "end": v(-149.41, 84.84) * mm});
            skArc(sketch, "E30.trimOffspring", {"start": v(-137.45, 103.1) * mm, "mid": v(-139, 101) * mm, "end": v(-140.53, 98.86) * mm});
            skArc(sketch, "E31.trimOffspring", {"start": v(-126.85, 115.89) * mm, "mid": v(-128.6, 113.94) * mm, "end": v(-130.33, 111.96) * mm});
            skArc(sketch, "E32.trimOffspring", {"start": v(-115.08, 127.59) * mm, "mid": v(-117.01, 125.82) * mm, "end": v(-118.92, 124.02) * mm});
            skArc(sketch, "E33.trimOffspring", {"start": v(-102.23, 138.1) * mm, "mid": v(-104.32, 136.52) * mm, "end": v(-106.4, 134.92) * mm});
            skArc(sketch, "E34.trimOffspring", {"start": v(-88.42, 147.32) * mm, "mid": v(-90.66, 145.95) * mm, "end": v(-92.88, 144.55) * mm});
            skArc(sketch, "E35.trimOffspring", {"start": v(-73.79, 155.17) * mm, "mid": v(-76.15, 154.02) * mm, "end": v(-78.5, 152.84) * mm});
            skArc(sketch, "E36.trimOffspring", {"start": v(-58.47, 161.56) * mm, "mid": v(-60.93, 160.65) * mm, "end": v(-63.37, 159.7) * mm});
            skArc(sketch, "E37.trimOffspring", {"start": v(-42.6, 166.45) * mm, "mid": v(-45.14, 165.78) * mm, "end": v(-47.66, 165.08) * mm});
            skArc(sketch, "E38.trimOffspring", {"start": v(-26.34, 169.79) * mm, "mid": v(-28.93, 169.37) * mm, "end": v(-31.5, 168.9) * mm});
            skArc(sketch, "E39.trimOffspring", {"start": v(-9.83, 171.54) * mm, "mid": v(-12.45, 171.37) * mm, "end": v(-15.06, 171.16) * mm});
            skArc(sketch, "E40.trimOffspring", {"start": v(6.77, 171.69) * mm, "mid": v(4.15, 171.77) * mm, "end": v(1.53, 171.81) * mm});
            skArc(sketch, "E41.trimOffspring", {"start": v(23.31, 170.23) * mm, "mid": v(20.71, 170.57) * mm, "end": v(18.1, 170.86) * mm});
            skArc(sketch, "E42.trimOffspring", {"start": v(39.63, 167.19) * mm, "mid": v(37.08, 167.77) * mm, "end": v(34.51, 168.32) * mm});
            skArc(sketch, "E43.trimOffspring", {"start": v(55.58, 162.58) * mm, "mid": v(53.1, 163.4) * mm, "end": v(50.6, 164.2) * mm});
            skArc(sketch, "E44.trimOffspring", {"start": v(71.01, 156.46) * mm, "mid": v(68.62, 157.52) * mm, "end": v(66.2, 158.55) * mm});
            skArc(sketch, "E45.trimOffspring", {"start": v(85.78, 148.87) * mm, "mid": v(83.5, 150.16) * mm, "end": v(81.2, 151.42) * mm});
            skArc(sketch, "E46.trimOffspring", {"start": v(99.75, 139.9) * mm, "mid": v(97.6, 141.4) * mm, "end": v(95.44, 142.88) * mm});
            skArc(sketch, "E47.trimOffspring", {"start": v(112.79, 129.62) * mm, "mid": v(110.8, 131.32) * mm, "end": v(108.78, 133) * mm});
            skArc(sketch, "E48.trimOffspring", {"start": v(124.77, 118.13) * mm, "mid": v(122.95, 120.02) * mm, "end": v(121.1, 121.88) * mm});
            skArc(sketch, "E49.trimOffspring", {"start": v(135.59, 105.53) * mm, "mid": v(133.96, 107.6) * mm, "end": v(132.3, 109.62) * mm});
            skArc(sketch, "E50.trimOffspring", {"start": v(145.14, 91.95) * mm, "mid": v(143.72, 94.16) * mm, "end": v(142.27, 96.34) * mm});
            skArc(sketch, "E51.trimOffspring", {"start": v(160.1, 62.36) * mm, "mid": v(159.13, 64.8) * mm, "end": v(158.13, 67.21) * mm});
            skArc(sketch, "E52.trimOffspring", {"start": v(165.38, 46.61) * mm, "mid": v(164.64, 49.13) * mm, "end": v(163.88, 51.64) * mm});
            skArc(sketch, "E53.trimOffspring", {"start": v(169.1, 30.43) * mm, "mid": v(168.62, 33.01) * mm, "end": v(168.1, 35.58) * mm});
            skArc(sketch, "E54.trimOffspring", {"start": v(171.25, 13.97) * mm, "mid": v(171.02, 16.58) * mm, "end": v(170.74, 19.2) * mm});
            skArc(sketch, "E55.trimOffspring", {"start": v(171.8, -2.62) * mm, "mid": v(171.82, 0) * mm, "end": v(171.8, 2.62) * mm});
            skArc(sketch, "E56.trimOffspring", {"start": v(170.74, -19.2) * mm, "mid": v(171.02, -16.58) * mm, "end": v(171.25, -13.97) * mm});
            skArc(sketch, "E57.trimOffspring", {"start": v(168.1, -35.58) * mm, "mid": v(168.62, -33.01) * mm, "end": v(169.1, -30.43) * mm});
            skArc(sketch, "E58.trimOffspring", {"start": v(163.88, -51.64) * mm, "mid": v(164.64, -49.13) * mm, "end": v(165.38, -46.61) * mm});
            skArc(sketch, "E59.trimOffspring", {"start": v(158.13, -67.21) * mm, "mid": v(159.13, -64.8) * mm, "end": v(160.1, -62.36) * mm});
            skArc(sketch, "E60.trimOffspring", {"start": v(150.9, -82.16) * mm, "mid": v(152.14, -79.85) * mm, "end": v(153.34, -77.52) * mm});
            skArc(sketch, "E61.trimOffspring", {"start": v(132.3, -109.62) * mm, "mid": v(133.96, -107.6) * mm, "end": v(135.59, -105.53) * mm});
            skArc(sketch, "E62.trimOffspring", {"start": v(121.1, -121.88) * mm, "mid": v(122.95, -120.02) * mm, "end": v(124.77, -118.13) * mm});
            skArc(sketch, "E63.trimOffspring", {"start": v(108.78, -133) * mm, "mid": v(110.8, -131.32) * mm, "end": v(112.79, -129.62) * mm});
            skArc(sketch, "E64.trimOffspring", {"start": v(95.44, -142.88) * mm, "mid": v(97.6, -141.4) * mm, "end": v(99.75, -139.9) * mm});
            skArc(sketch, "E65.trimOffspring", {"start": v(81.2, -151.42) * mm, "mid": v(83.5, -150.16) * mm, "end": v(85.78, -148.87) * mm});
            skArc(sketch, "E66.trimOffspring", {"start": v(66.2, -158.55) * mm, "mid": v(68.62, -157.52) * mm, "end": v(71.01, -156.46) * mm});
            skArc(sketch, "E67.trimOffspring", {"start": v(50.6, -164.2) * mm, "mid": v(53.1, -163.4) * mm, "end": v(55.58, -162.58) * mm});
            skArc(sketch, "E68.trimOffspring", {"start": v(34.51, -168.32) * mm, "mid": v(37.08, -167.77) * mm, "end": v(39.63, -167.19) * mm});
            skArc(sketch, "E69.trimOffspring", {"start": v(18.1, -170.86) * mm, "mid": v(20.71, -170.57) * mm, "end": v(23.31, -170.23) * mm});
            skArc(sketch, "E70.trimOffspring", {"start": v(1.53, -171.81) * mm, "mid": v(4.15, -171.77) * mm, "end": v(6.77, -171.69) * mm});
            skArc(sketch, "E71.trimOffspring", {"start": v(-15.06, -171.16) * mm, "mid": v(-12.45, -171.37) * mm, "end": v(-9.83, -171.54) * mm});
            skArc(sketch, "E72.trimOffspring", {"start": v(-31.5, -168.9) * mm, "mid": v(-28.93, -169.37) * mm, "end": v(-26.34, -169.79) * mm});
            skArc(sketch, "E73.trimOffspring", {"start": v(-47.66, -165.08) * mm, "mid": v(-45.14, -165.78) * mm, "end": v(-42.6, -166.45) * mm});
            skArc(sketch, "E74.trimOffspring", {"start": v(-63.37, -159.7) * mm, "mid": v(-60.93, -160.65) * mm, "end": v(-58.47, -161.56) * mm});
            skArc(sketch, "E75.trimOffspring", {"start": v(-78.5, -152.84) * mm, "mid": v(-76.15, -154.02) * mm, "end": v(-73.79, -155.17) * mm});
            skArc(sketch, "E76.trimOffspring", {"start": v(-92.88, -144.55) * mm, "mid": v(-90.66, -145.95) * mm, "end": v(-88.42, -147.32) * mm});
            skArc(sketch, "E77.trimOffspring", {"start": v(-106.4, -134.92) * mm, "mid": v(-104.32, -136.52) * mm, "end": v(-102.23, -138.1) * mm});
            skArc(sketch, "E78.trimOffspring", {"start": v(-118.92, -124.02) * mm, "mid": v(-117.01, -125.82) * mm, "end": v(-115.08, -127.59) * mm});
            skArc(sketch, "E79.trimOffspring", {"start": v(-130.33, -111.96) * mm, "mid": v(-128.6, -113.94) * mm, "end": v(-126.85, -115.89) * mm});
            skArc(sketch, "E80.trimOffspring", {"start": v(-140.53, -98.86) * mm, "mid": v(-139, -101) * mm, "end": v(-137.45, -103.1) * mm});
            skArc(sketch, "E81.trimOffspring", {"start": v(-149.41, -84.84) * mm, "mid": v(-148.1, -87.1) * mm, "end": v(-146.76, -89.36) * mm});
            skArc(sketch, "E82.trimOffspring", {"start": v(-156.9, -70.02) * mm, "mid": v(-155.82, -72.4) * mm, "end": v(-154.7, -74.77) * mm});
            skArc(sketch, "E83.trimOffspring", {"start": v(-162.93, -54.55) * mm, "mid": v(-162.08, -57.03) * mm, "end": v(-161.19, -59.5) * mm});
            skArc(sketch, "E84.trimOffspring", {"start": v(-167.43, -38.57) * mm, "mid": v(-166.83, -41.12) * mm, "end": v(-166.18, -43.66) * mm});
            skLineSegment(sketch, "E85", {"start": v(-169.62, -27.42) * mm, "end": v(-170.37, -22.23) * mm});
            skLineSegment(sketch, "E86", {"start": v(153.34, 77.52) * mm, "end": v(150.9, 82.16) * mm});
            skArc(sketch, "E87.trimOffspring", {"start": v(142.27, -96.34) * mm, "mid": v(143.72, -94.16) * mm, "end": v(145.14, -91.95) * mm});
            skSolve(sketch);
        }
        {
            var Q0;
            Q0=makeQuery(id+"F6.imprint","IMPRINT",FACE,{"disambiguationData":[TD([[makeQuery(id+"F6.imprint","IMPRINT",EDGE,{"derivedFrom":sQuery(id+"F6.wireOp",EDGE,"E13.left")}),1.0]])]});
            extrude(context, id + "F7", {"entities" : qUnion([Q0]), "operationType" : NewBodyOperationType.ADD, "oppositeDirection" : true, "depth" : 50 * mm});
        }
    });
